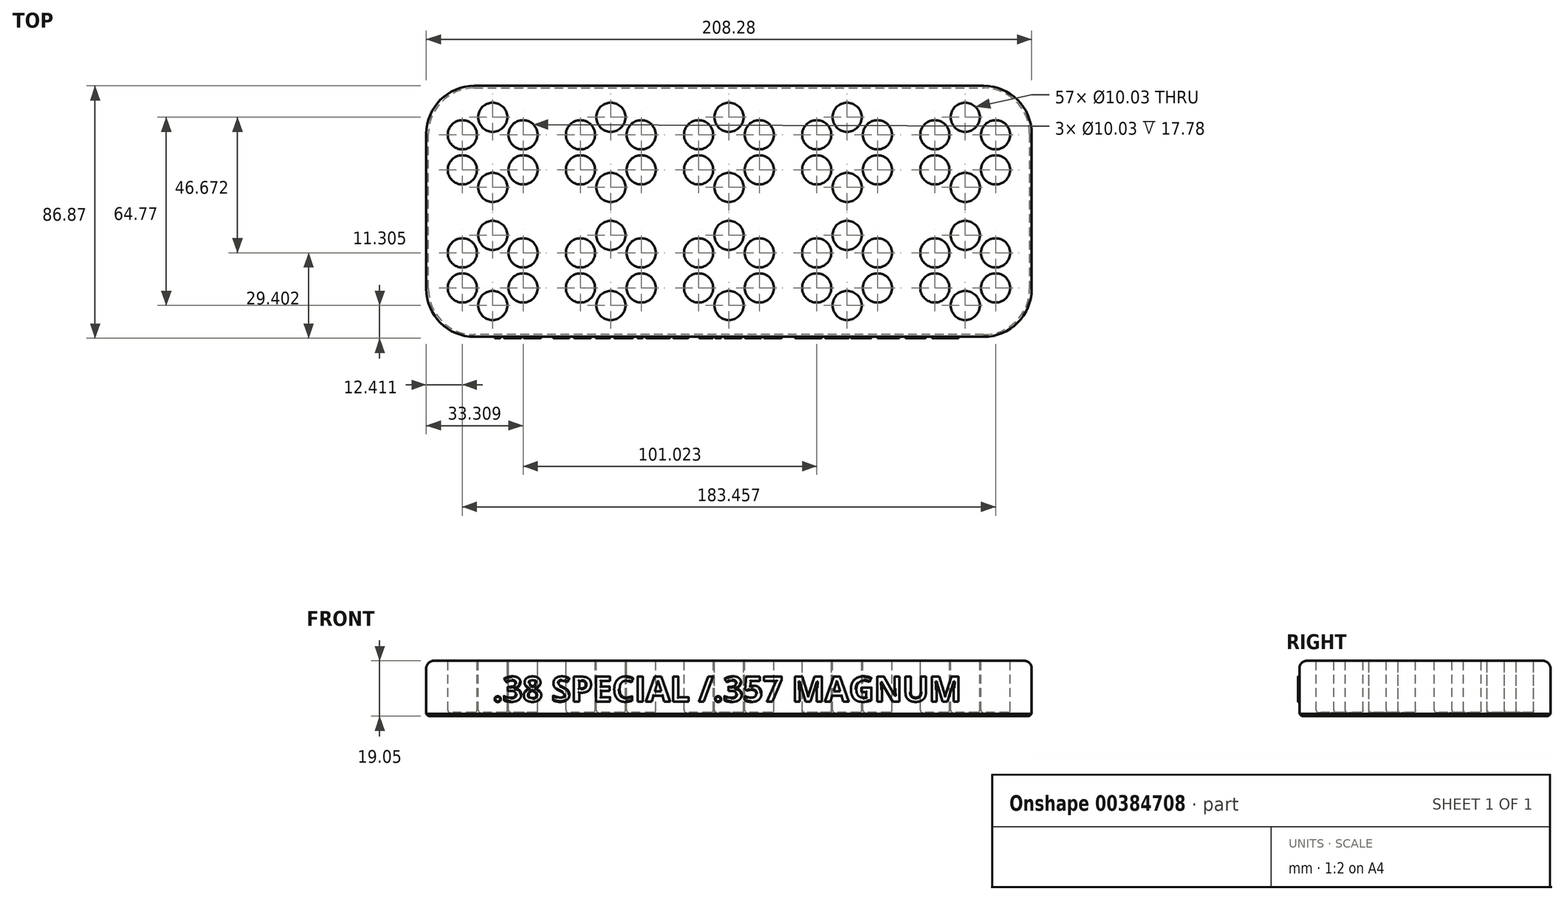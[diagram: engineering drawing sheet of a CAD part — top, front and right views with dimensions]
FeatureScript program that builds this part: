
annotation { "Feature Type Name" : "Feature", "Feature Type Description" : "" }
export const myFeature = defineFeature(function(context is Context, id is Id, definition is map)
    precondition{}
    {
        {
            var Q0;
            Q0=qCreatedBy(makeId("Top.planeOp"),FACE);
            var sketch = newSketch(context, id + "F0", { "sketchPlane" : qUnion([Q0])});
            skLineSegment(sketch, "E0.bottom", {"start": v(-106.68, 50.8) * mm, "end": v(101.6, 50.8) * mm});
            skLineSegment(sketch, "E0.top", {"start": v(-106.68, -35.56) * mm, "end": v(101.6, -35.56) * mm});
            skLineSegment(sketch, "E0.left", {"start": v(-106.68, 50.8) * mm, "end": v(-106.68, -35.56) * mm});
            skLineSegment(sketch, "E0.right", {"start": v(101.6, 50.8) * mm, "end": v(101.6, -35.56) * mm});
            skSolve(sketch);
        }
        {
            var Q0;
            Q0=qSketchRegion(id+"F0",true);
            extrude(context, id + "F1", {"entities" : qUnion([Q0]), "depth" : 19.05 * mm});
        }
        {
            var Q0;
            Q0=makeQuery(id+"F1.opExtrude","CAP_FACE",FACE,{"disambiguationData":[OSD([sQuery(id+"F0.wireOp",EDGE,"E0.bottom"),sQuery(id+"F0.wireOp",EDGE,"E0.top"),sQuery(id+"F0.wireOp",EDGE,"E0.left"),sQuery(id+"F0.wireOp",EDGE,"E0.right")])],"isStart":false});
            var sketch = newSketch(context, id + "F2", { "sketchPlane" : qUnion([Q0])});
            skCircle(sketch, "E1", {"center": v(-83.82, 27.94) * mm, "radius": 18.41 * mm});
            skCircle(sketch, "E2", {"center": v(-83.82, -12.7) * mm, "radius": 18.41 * mm});
            skCircle(sketch, "E3.1.0.0", {"center": v(-43.18, -12.7) * mm, "radius": 18.41 * mm});
            skCircle(sketch, "E3.1.0.1", {"center": v(-43.18, 27.94) * mm, "radius": 18.41 * mm});
            skCircle(sketch, "E3.2.0.0", {"center": v(-2.54, -12.7) * mm, "radius": 18.41 * mm});
            skCircle(sketch, "E3.2.0.1", {"center": v(-2.54, 27.94) * mm, "radius": 18.41 * mm});
            skCircle(sketch, "E3.3.0.0", {"center": v(38.1, -12.7) * mm, "radius": 18.41 * mm});
            skCircle(sketch, "E3.3.0.1", {"center": v(38.1, 27.94) * mm, "radius": 18.41 * mm});
            skCircle(sketch, "E3.4.0.0", {"center": v(78.74, -12.7) * mm, "radius": 18.41 * mm});
            skCircle(sketch, "E3.4.0.1", {"center": v(78.74, 27.94) * mm, "radius": 18.41 * mm});
            skLineSegment(sketch, "E3.direction1", {"start": v(-83.82, -12.7) * mm, "end": v(-43.18, -12.7) * mm, "construction": true});
            skSolve(sketch);
        }
        {
            var Q0;
            Q0=makeQuery(id+"F2.imprint","IMPRINT",FACE,{"disambiguationData":[TD([[makeQuery(id+"F2.imprint","IMPRINT",EDGE,{"derivedFrom":sQuery(id+"F2.wireOp",EDGE,"E1")}),-1.0]])]});
            var sketch = newSketch(context, id + "F3", { "sketchPlane" : qUnion([Q0])});
            skCircle(sketch, "E4", {"center": v(-83.82, 40) * mm, "radius": 5.02 * mm});
            skCircle(sketch, "E5.1.0", {"center": v(-94.27, 33.97) * mm, "radius": 5.02 * mm});
            skCircle(sketch, "E5.2.0", {"center": v(-94.27, 21.9) * mm, "radius": 5.02 * mm});
            skCircle(sketch, "E5.3.0", {"center": v(-83.82, 15.87) * mm, "radius": 5.02 * mm});
            skCircle(sketch, "E5.4.0", {"center": v(-73.37, 21.9) * mm, "radius": 5.02 * mm});
            skPoint(sketch, "E5.center", {"position": v(-83.82, 27.94) * mm});
            skCircle(sketch, "E6.1.5.0", {"center": v(-73.37, 33.97) * mm, "radius": 5.02 * mm});
            skCircle(sketch, "E7.0.1.0", {"center": v(-83.82, -0.64) * mm, "radius": 5.02 * mm});
            skCircle(sketch, "E7.0.1.1", {"center": v(-83.82, -24.77) * mm, "radius": 5.02 * mm});
            skCircle(sketch, "E7.0.1.2", {"center": v(-94.27, -6.67) * mm, "radius": 5.02 * mm});
            skCircle(sketch, "E7.0.1.3", {"center": v(-73.37, -18.73) * mm, "radius": 5.02 * mm});
            skPoint(sketch, "E7.0.1.4", {"position": v(-83.82, -12.7) * mm});
            skCircle(sketch, "E7.0.1.5", {"center": v(-94.27, -18.73) * mm, "radius": 5.02 * mm});
            skCircle(sketch, "E7.0.1.6", {"center": v(-73.37, -6.67) * mm, "radius": 5.02 * mm});
            skCircle(sketch, "E7.1.0.0", {"center": v(-43.18, 40) * mm, "radius": 5.02 * mm});
            skCircle(sketch, "E7.1.0.1", {"center": v(-43.18, 15.87) * mm, "radius": 5.02 * mm});
            skCircle(sketch, "E7.1.0.2", {"center": v(-53.63, 33.97) * mm, "radius": 5.02 * mm});
            skCircle(sketch, "E7.1.0.3", {"center": v(-32.73, 21.9) * mm, "radius": 5.02 * mm});
            skPoint(sketch, "E7.1.0.4", {"position": v(-43.18, 27.94) * mm});
            skCircle(sketch, "E7.1.0.5", {"center": v(-53.63, 21.9) * mm, "radius": 5.02 * mm});
            skCircle(sketch, "E7.1.0.6", {"center": v(-32.73, 33.97) * mm, "radius": 5.02 * mm});
            skCircle(sketch, "E7.1.1.0", {"center": v(-43.18, -0.64) * mm, "radius": 5.02 * mm});
            skCircle(sketch, "E7.1.1.1", {"center": v(-43.18, -24.77) * mm, "radius": 5.02 * mm});
            skCircle(sketch, "E7.1.1.2", {"center": v(-53.63, -6.67) * mm, "radius": 5.02 * mm});
            skCircle(sketch, "E7.1.1.3", {"center": v(-32.73, -18.73) * mm, "radius": 5.02 * mm});
            skPoint(sketch, "E7.1.1.4", {"position": v(-43.18, -12.7) * mm});
            skCircle(sketch, "E7.1.1.5", {"center": v(-53.63, -18.73) * mm, "radius": 5.02 * mm});
            skCircle(sketch, "E7.1.1.6", {"center": v(-32.73, -6.67) * mm, "radius": 5.02 * mm});
            skCircle(sketch, "E7.2.0.0", {"center": v(-2.54, 40) * mm, "radius": 5.02 * mm});
            skCircle(sketch, "E7.2.0.1", {"center": v(-2.54, 15.87) * mm, "radius": 5.02 * mm});
            skCircle(sketch, "E7.2.0.2", {"center": v(-12.99, 33.97) * mm, "radius": 5.02 * mm});
            skCircle(sketch, "E7.2.0.3", {"center": v(7.9, 21.9) * mm, "radius": 5.02 * mm});
            skPoint(sketch, "E7.2.0.4", {"position": v(-2.54, 27.94) * mm});
            skCircle(sketch, "E7.2.0.5", {"center": v(-12.99, 21.9) * mm, "radius": 5.02 * mm});
            skCircle(sketch, "E7.2.0.6", {"center": v(7.9, 33.97) * mm, "radius": 5.02 * mm});
            skCircle(sketch, "E7.2.1.0", {"center": v(-2.54, -0.64) * mm, "radius": 5.02 * mm});
            skCircle(sketch, "E7.2.1.1", {"center": v(-2.54, -24.77) * mm, "radius": 5.02 * mm});
            skCircle(sketch, "E7.2.1.2", {"center": v(-12.99, -6.67) * mm, "radius": 5.02 * mm});
            skCircle(sketch, "E7.2.1.3", {"center": v(7.9, -18.73) * mm, "radius": 5.02 * mm});
            skPoint(sketch, "E7.2.1.4", {"position": v(-2.54, -12.7) * mm});
            skCircle(sketch, "E7.2.1.5", {"center": v(-12.99, -18.73) * mm, "radius": 5.02 * mm});
            skCircle(sketch, "E7.2.1.6", {"center": v(7.9, -6.67) * mm, "radius": 5.02 * mm});
            skCircle(sketch, "E7.3.0.0", {"center": v(38.1, 40) * mm, "radius": 5.02 * mm});
            skCircle(sketch, "E7.3.0.1", {"center": v(38.1, 15.87) * mm, "radius": 5.02 * mm});
            skCircle(sketch, "E7.3.0.2", {"center": v(27.65, 33.97) * mm, "radius": 5.02 * mm});
            skCircle(sketch, "E7.3.0.3", {"center": v(48.55, 21.9) * mm, "radius": 5.02 * mm});
            skPoint(sketch, "E7.3.0.4", {"position": v(38.1, 27.94) * mm});
            skCircle(sketch, "E7.3.0.5", {"center": v(27.65, 21.9) * mm, "radius": 5.02 * mm});
            skCircle(sketch, "E7.3.0.6", {"center": v(48.55, 33.97) * mm, "radius": 5.02 * mm});
            skCircle(sketch, "E7.3.1.0", {"center": v(38.1, -0.64) * mm, "radius": 5.02 * mm});
            skCircle(sketch, "E7.3.1.1", {"center": v(38.1, -24.77) * mm, "radius": 5.02 * mm});
            skCircle(sketch, "E7.3.1.2", {"center": v(27.65, -6.67) * mm, "radius": 5.02 * mm});
            skCircle(sketch, "E7.3.1.3", {"center": v(48.55, -18.73) * mm, "radius": 5.02 * mm});
            skPoint(sketch, "E7.3.1.4", {"position": v(38.1, -12.7) * mm});
            skCircle(sketch, "E7.3.1.5", {"center": v(27.65, -18.73) * mm, "radius": 5.02 * mm});
            skCircle(sketch, "E7.3.1.6", {"center": v(48.55, -6.67) * mm, "radius": 5.02 * mm});
            skCircle(sketch, "E7.4.0.0", {"center": v(78.74, 40) * mm, "radius": 5.02 * mm});
            skCircle(sketch, "E7.4.0.1", {"center": v(78.74, 15.87) * mm, "radius": 5.02 * mm});
            skCircle(sketch, "E7.4.0.2", {"center": v(68.3, 33.97) * mm, "radius": 5.02 * mm});
            skCircle(sketch, "E7.4.0.3", {"center": v(89.19, 21.9) * mm, "radius": 5.02 * mm});
            skPoint(sketch, "E7.4.0.4", {"position": v(78.74, 27.94) * mm});
            skCircle(sketch, "E7.4.0.5", {"center": v(68.3, 21.9) * mm, "radius": 5.02 * mm});
            skCircle(sketch, "E7.4.0.6", {"center": v(89.19, 33.97) * mm, "radius": 5.02 * mm});
            skCircle(sketch, "E7.4.1.0", {"center": v(78.74, -0.64) * mm, "radius": 5.02 * mm});
            skCircle(sketch, "E7.4.1.1", {"center": v(78.74, -24.77) * mm, "radius": 5.02 * mm});
            skCircle(sketch, "E7.4.1.2", {"center": v(68.3, -6.67) * mm, "radius": 5.02 * mm});
            skCircle(sketch, "E7.4.1.3", {"center": v(89.19, -18.73) * mm, "radius": 5.02 * mm});
            skPoint(sketch, "E7.4.1.4", {"position": v(78.74, -12.7) * mm});
            skCircle(sketch, "E7.4.1.5", {"center": v(68.3, -18.73) * mm, "radius": 5.02 * mm});
            skCircle(sketch, "E7.4.1.6", {"center": v(89.19, -6.67) * mm, "radius": 5.02 * mm});
            skLineSegment(sketch, "E7.direction1", {"start": v(-94.27, 21.9) * mm, "end": v(-53.63, 21.9) * mm, "construction": true});
            skLineSegment(sketch, "E7.direction2", {"start": v(-94.27, 21.9) * mm, "end": v(-94.27, -18.73) * mm, "construction": true});
            skSolve(sketch);
        }
        {
            var Q0;
            Q0=qSketchRegion(id+"F3",true);
            extrude(context, id + "F4", {"entities" : qUnion([Q0]), "operationType" : NewBodyOperationType.REMOVE, "oppositeDirection" : true, "depth" : 17.78 * mm});
        }
        {
            var Q0;
            Q0=makeQuery(id+"F1.opExtrude","SWEPT_EDGE",EDGE,{"disambiguationData":[OSD([sQuery(id+"F0.wireOp",EDGE,"E0.top"),sQuery(id+"F0.wireOp",EDGE,"E0.left")])]});
            var Q1;
            Q1=makeQuery(id+"F1.opExtrude","SWEPT_EDGE",EDGE,{"disambiguationData":[OSD([sQuery(id+"F0.wireOp",EDGE,"E0.bottom"),sQuery(id+"F0.wireOp",EDGE,"E0.left")])]});
            var Q2;
            Q2=makeQuery(id+"F1.opExtrude","SWEPT_EDGE",EDGE,{"disambiguationData":[OSD([sQuery(id+"F0.wireOp",EDGE,"E0.bottom"),sQuery(id+"F0.wireOp",EDGE,"E0.right")])]});
            var Q3;
            Q3=makeQuery(id+"F1.opExtrude","SWEPT_EDGE",EDGE,{"disambiguationData":[OSD([sQuery(id+"F0.wireOp",EDGE,"E0.top"),sQuery(id+"F0.wireOp",EDGE,"E0.right")])]});
            fillet(context, id + "F5", {"entities" : qUnion([Q0, Q1, Q2, Q3]), "radius" : 16.5 * mm, "tangentPropagation" : true, "allowEdgeOverflow" : false});
        }
        {
            var Q0;
            Q0=makeQuery(id+"F1.opExtrude","CAP_EDGE",EDGE,{"disambiguationData":[OSD([sQuery(id+"F0.wireOp",EDGE,"E0.bottom")])],"isStart":false});
            fillet(context, id + "F6", {"entities" : qUnion([Q0]), "radius" : 2.54 * mm, "tangentPropagation" : true, "allowEdgeOverflow" : false});
        }
        {
            var Q0;
            Q0=makeQuery(id+"F4.boolean.opBoolean","COPY",EDGE,{"derivedFrom":makeQuery(id+"F4.opExtrude","CAP_EDGE",EDGE,{"disambiguationData":[OSD([sQuery(id+"F3.wireOp",EDGE,"d77acf85-acbb-40a3-aece-45e6eb51fefa.2.0.3")])],"isStart":true})});
            var Q1;
            Q1=makeQuery(id+"F4.boolean.opBoolean","COPY",EDGE,{"derivedFrom":makeQuery(id+"F4.opExtrude","CAP_EDGE",EDGE,{"disambiguationData":[OSD([sQuery(id+"F3.wireOp",EDGE,"d77acf85-acbb-40a3-aece-45e6eb51fefa.1.0.3")])],"isStart":true})});
            var Q2;
            Q2=makeQuery(id+"F4.boolean.opBoolean","COPY",EDGE,{"derivedFrom":makeQuery(id+"F4.opExtrude","CAP_EDGE",EDGE,{"disambiguationData":[OSD([sQuery(id+"F3.wireOp",EDGE,"d77acf85-acbb-40a3-aece-45e6eb51fefa.4.0.3")])],"isStart":true})});
            var Q3;
            Q3=makeQuery(id+"F4.boolean.opBoolean","COPY",EDGE,{"derivedFrom":makeQuery(id+"F4.opExtrude","CAP_EDGE",EDGE,{"disambiguationData":[OSD([sQuery(id+"F3.wireOp",EDGE,"d77acf85-acbb-40a3-aece-45e6eb51fefa.4.1.0")])],"isStart":true})});
            var Q4;
            Q4=makeQuery(id+"F4.boolean.opBoolean","COPY",EDGE,{"derivedFrom":makeQuery(id+"F4.opExtrude","CAP_EDGE",EDGE,{"disambiguationData":[OSD([sQuery(id+"F3.wireOp",EDGE,"d77acf85-acbb-40a3-aece-45e6eb51fefa.4.0.2")])],"isStart":true})});
            var Q5;
            Q5=makeQuery(id+"F4.boolean.opBoolean","COPY",EDGE,{"derivedFrom":makeQuery(id+"F4.opExtrude","CAP_EDGE",EDGE,{"disambiguationData":[OSD([sQuery(id+"F3.wireOp",EDGE,"d77acf85-acbb-40a3-aece-45e6eb51fefa.4.0.0")])],"isStart":true})});
            var Q6;
            Q6=makeQuery(id+"F4.boolean.opBoolean","COPY",EDGE,{"derivedFrom":makeQuery(id+"F4.opExtrude","CAP_EDGE",EDGE,{"disambiguationData":[OSD([sQuery(id+"F3.wireOp",EDGE,"d77acf85-acbb-40a3-aece-45e6eb51fefa.0.1.5")])],"isStart":true})});
            var Q7;
            Q7=makeQuery(id+"F4.boolean.opBoolean","COPY",EDGE,{"derivedFrom":makeQuery(id+"F4.opExtrude","CAP_EDGE",EDGE,{"disambiguationData":[OSD([sQuery(id+"F3.wireOp",EDGE,"d77acf85-acbb-40a3-aece-45e6eb51fefa.2.0.0")])],"isStart":true})});
            var Q8;
            Q8=makeQuery(id+"F4.boolean.opBoolean","COPY",EDGE,{"derivedFrom":makeQuery(id+"F4.opExtrude","CAP_EDGE",EDGE,{"disambiguationData":[OSD([sQuery(id+"F3.wireOp",EDGE,"E4")])],"isStart":true})});
            var Q9;
            Q9=makeQuery(id+"F4.boolean.opBoolean","COPY",EDGE,{"derivedFrom":makeQuery(id+"F4.opExtrude","CAP_EDGE",EDGE,{"disambiguationData":[OSD([sQuery(id+"F3.wireOp",EDGE,"d77acf85-acbb-40a3-aece-45e6eb51fefa.2.1.0")])],"isStart":true})});
            var Q10;
            Q10=makeQuery(id+"F4.boolean.opBoolean","COPY",EDGE,{"derivedFrom":makeQuery(id+"F4.opExtrude","CAP_EDGE",EDGE,{"disambiguationData":[OSD([sQuery(id+"F3.wireOp",EDGE,"d77acf85-acbb-40a3-aece-45e6eb51fefa.1.1.3")])],"isStart":true})});
            var Q11;
            Q11=makeQuery(id+"F4.boolean.opBoolean","COPY",EDGE,{"derivedFrom":makeQuery(id+"F4.opExtrude","CAP_EDGE",EDGE,{"disambiguationData":[OSD([sQuery(id+"F3.wireOp",EDGE,"d77acf85-acbb-40a3-aece-45e6eb51fefa.2.1.2")])],"isStart":true})});
            var Q12;
            Q12=makeQuery(id+"F4.boolean.opBoolean","COPY",EDGE,{"derivedFrom":makeQuery(id+"F4.opExtrude","CAP_EDGE",EDGE,{"disambiguationData":[OSD([sQuery(id+"F3.wireOp",EDGE,"E5.4.0")])],"isStart":true})});
            var Q13;
            Q13=makeQuery(id+"F4.boolean.opBoolean","COPY",EDGE,{"derivedFrom":makeQuery(id+"F4.opExtrude","CAP_EDGE",EDGE,{"disambiguationData":[OSD([sQuery(id+"F3.wireOp",EDGE,"E5.3.0")])],"isStart":true})});
            var Q14;
            Q14=makeQuery(id+"F4.boolean.opBoolean","COPY",EDGE,{"derivedFrom":makeQuery(id+"F4.opExtrude","CAP_EDGE",EDGE,{"disambiguationData":[OSD([sQuery(id+"F3.wireOp",EDGE,"d77acf85-acbb-40a3-aece-45e6eb51fefa.3.1.4")])],"isStart":true})});
            var Q15;
            Q15=makeQuery(id+"F4.boolean.opBoolean","COPY",EDGE,{"derivedFrom":makeQuery(id+"F4.opExtrude","CAP_EDGE",EDGE,{"disambiguationData":[OSD([sQuery(id+"F3.wireOp",EDGE,"d77acf85-acbb-40a3-aece-45e6eb51fefa.1.0.5")])],"isStart":true})});
            var Q16;
            Q16=makeQuery(id+"F4.boolean.opBoolean","COPY",EDGE,{"derivedFrom":makeQuery(id+"F4.opExtrude","CAP_EDGE",EDGE,{"disambiguationData":[OSD([sQuery(id+"F3.wireOp",EDGE,"d77acf85-acbb-40a3-aece-45e6eb51fefa.1.0.4")])],"isStart":true})});
            var Q17;
            Q17=makeQuery(id+"F4.boolean.opBoolean","COPY",EDGE,{"derivedFrom":makeQuery(id+"F4.opExtrude","CAP_EDGE",EDGE,{"disambiguationData":[OSD([sQuery(id+"F3.wireOp",EDGE,"d77acf85-acbb-40a3-aece-45e6eb51fefa.2.1.3")])],"isStart":true})});
            var Q18;
            Q18=makeQuery(id+"F4.boolean.opBoolean","COPY",EDGE,{"derivedFrom":makeQuery(id+"F4.opExtrude","CAP_EDGE",EDGE,{"disambiguationData":[OSD([sQuery(id+"F3.wireOp",EDGE,"d77acf85-acbb-40a3-aece-45e6eb51fefa.1.1.4")])],"isStart":true})});
            var Q19;
            Q19=makeQuery(id+"F4.boolean.opBoolean","COPY",EDGE,{"derivedFrom":makeQuery(id+"F4.opExtrude","CAP_EDGE",EDGE,{"disambiguationData":[OSD([sQuery(id+"F3.wireOp",EDGE,"d77acf85-acbb-40a3-aece-45e6eb51fefa.3.0.2")])],"isStart":true})});
            var Q20;
            Q20=makeQuery(id+"F4.boolean.opBoolean","COPY",EDGE,{"derivedFrom":makeQuery(id+"F4.opExtrude","CAP_EDGE",EDGE,{"disambiguationData":[OSD([sQuery(id+"F3.wireOp",EDGE,"d77acf85-acbb-40a3-aece-45e6eb51fefa.3.1.5")])],"isStart":true})});
            var Q21;
            Q21=makeQuery(id+"F4.boolean.opBoolean","COPY",EDGE,{"derivedFrom":makeQuery(id+"F4.opExtrude","CAP_EDGE",EDGE,{"disambiguationData":[OSD([sQuery(id+"F3.wireOp",EDGE,"d77acf85-acbb-40a3-aece-45e6eb51fefa.4.1.3")])],"isStart":true})});
            var Q22;
            Q22=makeQuery(id+"F4.boolean.opBoolean","COPY",EDGE,{"derivedFrom":makeQuery(id+"F4.opExtrude","CAP_EDGE",EDGE,{"disambiguationData":[OSD([sQuery(id+"F3.wireOp",EDGE,"d77acf85-acbb-40a3-aece-45e6eb51fefa.2.1.5")])],"isStart":true})});
            var Q23;
            Q23=makeQuery(id+"F4.boolean.opBoolean","COPY",EDGE,{"derivedFrom":makeQuery(id+"F4.opExtrude","CAP_EDGE",EDGE,{"disambiguationData":[OSD([sQuery(id+"F3.wireOp",EDGE,"d77acf85-acbb-40a3-aece-45e6eb51fefa.4.1.2")])],"isStart":true})});
            var Q24;
            Q24=makeQuery(id+"F4.boolean.opBoolean","COPY",EDGE,{"derivedFrom":makeQuery(id+"F4.opExtrude","CAP_EDGE",EDGE,{"disambiguationData":[OSD([sQuery(id+"F3.wireOp",EDGE,"d77acf85-acbb-40a3-aece-45e6eb51fefa.2.0.2")])],"isStart":true})});
            var Q25;
            Q25=makeQuery(id+"F4.boolean.opBoolean","COPY",EDGE,{"derivedFrom":makeQuery(id+"F4.opExtrude","CAP_EDGE",EDGE,{"disambiguationData":[OSD([sQuery(id+"F3.wireOp",EDGE,"d77acf85-acbb-40a3-aece-45e6eb51fefa.1.1.5")])],"isStart":true})});
            var Q26;
            Q26=makeQuery(id+"F4.boolean.opBoolean","COPY",EDGE,{"derivedFrom":makeQuery(id+"F4.opExtrude","CAP_EDGE",EDGE,{"disambiguationData":[OSD([sQuery(id+"F3.wireOp",EDGE,"d77acf85-acbb-40a3-aece-45e6eb51fefa.3.0.0")])],"isStart":true})});
            var Q27;
            Q27=makeQuery(id+"F4.boolean.opBoolean","COPY",EDGE,{"derivedFrom":makeQuery(id+"F4.opExtrude","CAP_EDGE",EDGE,{"disambiguationData":[OSD([sQuery(id+"F3.wireOp",EDGE,"d77acf85-acbb-40a3-aece-45e6eb51fefa.2.0.5")])],"isStart":true})});
            var Q28;
            Q28=makeQuery(id+"F4.boolean.opBoolean","COPY",EDGE,{"derivedFrom":makeQuery(id+"F4.opExtrude","CAP_EDGE",EDGE,{"disambiguationData":[OSD([sQuery(id+"F3.wireOp",EDGE,"d77acf85-acbb-40a3-aece-45e6eb51fefa.0.1.0")])],"isStart":true})});
            var Q29;
            Q29=makeQuery(id+"F4.boolean.opBoolean","COPY",EDGE,{"derivedFrom":makeQuery(id+"F4.opExtrude","CAP_EDGE",EDGE,{"disambiguationData":[OSD([sQuery(id+"F3.wireOp",EDGE,"d77acf85-acbb-40a3-aece-45e6eb51fefa.4.0.4")])],"isStart":true})});
            var Q30;
            Q30=makeQuery(id+"F4.boolean.opBoolean","COPY",EDGE,{"derivedFrom":makeQuery(id+"F4.opExtrude","CAP_EDGE",EDGE,{"disambiguationData":[OSD([sQuery(id+"F3.wireOp",EDGE,"d77acf85-acbb-40a3-aece-45e6eb51fefa.4.0.5")])],"isStart":true})});
            var Q31;
            Q31=makeQuery(id+"F4.boolean.opBoolean","COPY",EDGE,{"derivedFrom":makeQuery(id+"F4.opExtrude","CAP_EDGE",EDGE,{"disambiguationData":[OSD([sQuery(id+"F3.wireOp",EDGE,"d77acf85-acbb-40a3-aece-45e6eb51fefa.3.0.3")])],"isStart":true})});
            var Q32;
            Q32=makeQuery(id+"F4.boolean.opBoolean","COPY",EDGE,{"derivedFrom":makeQuery(id+"F4.opExtrude","CAP_EDGE",EDGE,{"disambiguationData":[OSD([sQuery(id+"F3.wireOp",EDGE,"d77acf85-acbb-40a3-aece-45e6eb51fefa.4.1.4")])],"isStart":true})});
            var Q33;
            Q33=makeQuery(id+"F4.boolean.opBoolean","COPY",EDGE,{"derivedFrom":makeQuery(id+"F4.opExtrude","CAP_EDGE",EDGE,{"disambiguationData":[OSD([sQuery(id+"F3.wireOp",EDGE,"d77acf85-acbb-40a3-aece-45e6eb51fefa.3.1.2")])],"isStart":true})});
            var Q34;
            Q34=makeQuery(id+"F4.boolean.opBoolean","COPY",EDGE,{"derivedFrom":makeQuery(id+"F4.opExtrude","CAP_EDGE",EDGE,{"disambiguationData":[OSD([sQuery(id+"F3.wireOp",EDGE,"E5.2.0")])],"isStart":true})});
            var Q35;
            Q35=makeQuery(id+"F4.boolean.opBoolean","COPY",EDGE,{"derivedFrom":makeQuery(id+"F4.opExtrude","CAP_EDGE",EDGE,{"disambiguationData":[OSD([sQuery(id+"F3.wireOp",EDGE,"d77acf85-acbb-40a3-aece-45e6eb51fefa.0.1.2")])],"isStart":true})});
            var Q36;
            Q36=makeQuery(id+"F4.boolean.opBoolean","COPY",EDGE,{"derivedFrom":makeQuery(id+"F4.opExtrude","CAP_EDGE",EDGE,{"disambiguationData":[OSD([sQuery(id+"F3.wireOp",EDGE,"d77acf85-acbb-40a3-aece-45e6eb51fefa.1.0.2")])],"isStart":true})});
            var Q37;
            Q37=makeQuery(id+"F4.boolean.opBoolean","COPY",EDGE,{"derivedFrom":makeQuery(id+"F4.opExtrude","CAP_EDGE",EDGE,{"disambiguationData":[OSD([sQuery(id+"F3.wireOp",EDGE,"d77acf85-acbb-40a3-aece-45e6eb51fefa.1.1.0")])],"isStart":true})});
            var Q38;
            Q38=makeQuery(id+"F4.boolean.opBoolean","COPY",EDGE,{"derivedFrom":makeQuery(id+"F4.opExtrude","CAP_EDGE",EDGE,{"disambiguationData":[OSD([sQuery(id+"F3.wireOp",EDGE,"d77acf85-acbb-40a3-aece-45e6eb51fefa.2.0.4")])],"isStart":true})});
            var Q39;
            Q39=makeQuery(id+"F4.boolean.opBoolean","COPY",EDGE,{"derivedFrom":makeQuery(id+"F4.opExtrude","CAP_EDGE",EDGE,{"disambiguationData":[OSD([sQuery(id+"F3.wireOp",EDGE,"d77acf85-acbb-40a3-aece-45e6eb51fefa.2.1.4")])],"isStart":true})});
            var Q40;
            Q40=makeQuery(id+"F4.boolean.opBoolean","COPY",EDGE,{"derivedFrom":makeQuery(id+"F4.opExtrude","CAP_EDGE",EDGE,{"disambiguationData":[OSD([sQuery(id+"F3.wireOp",EDGE,"d77acf85-acbb-40a3-aece-45e6eb51fefa.1.0.0")])],"isStart":true})});
            var Q41;
            Q41=makeQuery(id+"F4.boolean.opBoolean","COPY",EDGE,{"derivedFrom":makeQuery(id+"F4.opExtrude","CAP_EDGE",EDGE,{"disambiguationData":[OSD([sQuery(id+"F3.wireOp",EDGE,"d77acf85-acbb-40a3-aece-45e6eb51fefa.1.1.2")])],"isStart":true})});
            var Q42;
            Q42=makeQuery(id+"F4.boolean.opBoolean","COPY",EDGE,{"derivedFrom":makeQuery(id+"F4.opExtrude","CAP_EDGE",EDGE,{"disambiguationData":[OSD([sQuery(id+"F3.wireOp",EDGE,"d77acf85-acbb-40a3-aece-45e6eb51fefa.0.1.3")])],"isStart":true})});
            var Q43;
            Q43=makeQuery(id+"F4.boolean.opBoolean","COPY",EDGE,{"derivedFrom":makeQuery(id+"F4.opExtrude","CAP_EDGE",EDGE,{"disambiguationData":[OSD([sQuery(id+"F3.wireOp",EDGE,"d77acf85-acbb-40a3-aece-45e6eb51fefa.4.1.5")])],"isStart":true})});
            var Q44;
            Q44=makeQuery(id+"F4.boolean.opBoolean","COPY",EDGE,{"derivedFrom":makeQuery(id+"F4.opExtrude","CAP_EDGE",EDGE,{"disambiguationData":[OSD([sQuery(id+"F3.wireOp",EDGE,"d77acf85-acbb-40a3-aece-45e6eb51fefa.3.0.4")])],"isStart":true})});
            var Q45;
            Q45=makeQuery(id+"F4.boolean.opBoolean","COPY",EDGE,{"derivedFrom":makeQuery(id+"F4.opExtrude","CAP_EDGE",EDGE,{"disambiguationData":[OSD([sQuery(id+"F3.wireOp",EDGE,"d77acf85-acbb-40a3-aece-45e6eb51fefa.3.0.5")])],"isStart":true})});
            var Q46;
            Q46=makeQuery(id+"F4.boolean.opBoolean","COPY",EDGE,{"derivedFrom":makeQuery(id+"F4.opExtrude","CAP_EDGE",EDGE,{"disambiguationData":[OSD([sQuery(id+"F3.wireOp",EDGE,"d77acf85-acbb-40a3-aece-45e6eb51fefa.3.1.0")])],"isStart":true})});
            var Q47;
            Q47=makeQuery(id+"F4.boolean.opBoolean","COPY",EDGE,{"derivedFrom":makeQuery(id+"F4.opExtrude","CAP_EDGE",EDGE,{"disambiguationData":[OSD([sQuery(id+"F3.wireOp",EDGE,"d77acf85-acbb-40a3-aece-45e6eb51fefa.3.1.3")])],"isStart":true})});
            var Q48;
            Q48=makeQuery(id+"F4.boolean.opBoolean","COPY",EDGE,{"derivedFrom":makeQuery(id+"F4.opExtrude","CAP_EDGE",EDGE,{"disambiguationData":[OSD([sQuery(id+"F3.wireOp",EDGE,"d77acf85-acbb-40a3-aece-45e6eb51fefa.0.1.2")])],"isStart":false})});
            var Q49;
            Q49=makeQuery(id+"F4.boolean.opBoolean","COPY",EDGE,{"derivedFrom":makeQuery(id+"F4.opExtrude","CAP_EDGE",EDGE,{"disambiguationData":[OSD([sQuery(id+"F3.wireOp",EDGE,"d77acf85-acbb-40a3-aece-45e6eb51fefa.0.1.3")])],"isStart":false})});
            var Q50;
            Q50=makeQuery(id+"F4.boolean.opBoolean","COPY",EDGE,{"derivedFrom":makeQuery(id+"F4.opExtrude","CAP_EDGE",EDGE,{"disambiguationData":[OSD([sQuery(id+"F3.wireOp",EDGE,"E4")])],"isStart":false})});
            var Q51;
            Q51=makeQuery(id+"F4.boolean.opBoolean","COPY",EDGE,{"derivedFrom":makeQuery(id+"F4.opExtrude","CAP_EDGE",EDGE,{"disambiguationData":[OSD([sQuery(id+"F3.wireOp",EDGE,"E5.2.0")])],"isStart":false})});
            var Q52;
            Q52=makeQuery(id+"F4.boolean.opBoolean","COPY",EDGE,{"derivedFrom":makeQuery(id+"F4.opExtrude","CAP_EDGE",EDGE,{"disambiguationData":[OSD([sQuery(id+"F3.wireOp",EDGE,"E5.3.0")])],"isStart":false})});
            var Q53;
            Q53=makeQuery(id+"F4.boolean.opBoolean","COPY",EDGE,{"derivedFrom":makeQuery(id+"F4.opExtrude","CAP_EDGE",EDGE,{"disambiguationData":[OSD([sQuery(id+"F3.wireOp",EDGE,"E5.4.0")])],"isStart":false})});
            var Q54;
            Q54=makeQuery(id+"F4.boolean.opBoolean","COPY",EDGE,{"derivedFrom":makeQuery(id+"F4.opExtrude","CAP_EDGE",EDGE,{"disambiguationData":[OSD([sQuery(id+"F3.wireOp",EDGE,"d77acf85-acbb-40a3-aece-45e6eb51fefa.0.1.0")])],"isStart":false})});
            var Q55;
            Q55=makeQuery(id+"F4.boolean.opBoolean","COPY",EDGE,{"derivedFrom":makeQuery(id+"F4.opExtrude","CAP_EDGE",EDGE,{"disambiguationData":[OSD([sQuery(id+"F3.wireOp",EDGE,"d77acf85-acbb-40a3-aece-45e6eb51fefa.1.0.5")])],"isStart":false})});
            var Q56;
            Q56=makeQuery(id+"F4.boolean.opBoolean","COPY",EDGE,{"derivedFrom":makeQuery(id+"F4.opExtrude","CAP_EDGE",EDGE,{"disambiguationData":[OSD([sQuery(id+"F3.wireOp",EDGE,"d77acf85-acbb-40a3-aece-45e6eb51fefa.2.0.3")])],"isStart":false})});
            var Q57;
            Q57=makeQuery(id+"F4.boolean.opBoolean","COPY",EDGE,{"derivedFrom":makeQuery(id+"F4.opExtrude","CAP_EDGE",EDGE,{"disambiguationData":[OSD([sQuery(id+"F3.wireOp",EDGE,"d77acf85-acbb-40a3-aece-45e6eb51fefa.3.0.0")])],"isStart":false})});
            var Q58;
            Q58=makeQuery(id+"F4.boolean.opBoolean","COPY",EDGE,{"derivedFrom":makeQuery(id+"F4.opExtrude","CAP_EDGE",EDGE,{"disambiguationData":[OSD([sQuery(id+"F3.wireOp",EDGE,"d77acf85-acbb-40a3-aece-45e6eb51fefa.3.1.4")])],"isStart":false})});
            var Q59;
            Q59=makeQuery(id+"F4.boolean.opBoolean","COPY",EDGE,{"derivedFrom":makeQuery(id+"F4.opExtrude","CAP_EDGE",EDGE,{"disambiguationData":[OSD([sQuery(id+"F3.wireOp",EDGE,"d77acf85-acbb-40a3-aece-45e6eb51fefa.4.1.2")])],"isStart":false})});
            var Q60;
            Q60=makeQuery(id+"F4.boolean.opBoolean","COPY",EDGE,{"derivedFrom":makeQuery(id+"F4.opExtrude","CAP_EDGE",EDGE,{"disambiguationData":[OSD([sQuery(id+"F3.wireOp",EDGE,"d77acf85-acbb-40a3-aece-45e6eb51fefa.1.1.0")])],"isStart":false})});
            var Q61;
            Q61=makeQuery(id+"F4.boolean.opBoolean","COPY",EDGE,{"derivedFrom":makeQuery(id+"F4.opExtrude","CAP_EDGE",EDGE,{"disambiguationData":[OSD([sQuery(id+"F3.wireOp",EDGE,"d77acf85-acbb-40a3-aece-45e6eb51fefa.2.0.4")])],"isStart":false})});
            var Q62;
            Q62=makeQuery(id+"F4.boolean.opBoolean","COPY",EDGE,{"derivedFrom":makeQuery(id+"F4.opExtrude","CAP_EDGE",EDGE,{"disambiguationData":[OSD([sQuery(id+"F3.wireOp",EDGE,"d77acf85-acbb-40a3-aece-45e6eb51fefa.3.0.2")])],"isStart":false})});
            var Q63;
            Q63=makeQuery(id+"F4.boolean.opBoolean","COPY",EDGE,{"derivedFrom":makeQuery(id+"F4.opExtrude","CAP_EDGE",EDGE,{"disambiguationData":[OSD([sQuery(id+"F3.wireOp",EDGE,"d77acf85-acbb-40a3-aece-45e6eb51fefa.3.1.5")])],"isStart":false})});
            var Q64;
            Q64=makeQuery(id+"F4.boolean.opBoolean","COPY",EDGE,{"derivedFrom":makeQuery(id+"F4.opExtrude","CAP_EDGE",EDGE,{"disambiguationData":[OSD([sQuery(id+"F3.wireOp",EDGE,"d77acf85-acbb-40a3-aece-45e6eb51fefa.4.1.3")])],"isStart":false})});
            var Q65;
            Q65=makeQuery(id+"F4.boolean.opBoolean","COPY",EDGE,{"derivedFrom":makeQuery(id+"F4.opExtrude","CAP_EDGE",EDGE,{"disambiguationData":[OSD([sQuery(id+"F3.wireOp",EDGE,"d77acf85-acbb-40a3-aece-45e6eb51fefa.1.1.2")])],"isStart":false})});
            var Q66;
            Q66=makeQuery(id+"F4.boolean.opBoolean","COPY",EDGE,{"derivedFrom":makeQuery(id+"F4.opExtrude","CAP_EDGE",EDGE,{"disambiguationData":[OSD([sQuery(id+"F3.wireOp",EDGE,"d77acf85-acbb-40a3-aece-45e6eb51fefa.2.0.5")])],"isStart":false})});
            var Q67;
            Q67=makeQuery(id+"F4.boolean.opBoolean","COPY",EDGE,{"derivedFrom":makeQuery(id+"F4.opExtrude","CAP_EDGE",EDGE,{"disambiguationData":[OSD([sQuery(id+"F3.wireOp",EDGE,"d77acf85-acbb-40a3-aece-45e6eb51fefa.3.0.3")])],"isStart":false})});
            var Q68;
            Q68=makeQuery(id+"F4.boolean.opBoolean","COPY",EDGE,{"derivedFrom":makeQuery(id+"F4.opExtrude","CAP_EDGE",EDGE,{"disambiguationData":[OSD([sQuery(id+"F3.wireOp",EDGE,"d77acf85-acbb-40a3-aece-45e6eb51fefa.4.0.0")])],"isStart":false})});
            var Q69;
            Q69=makeQuery(id+"F4.boolean.opBoolean","COPY",EDGE,{"derivedFrom":makeQuery(id+"F4.opExtrude","CAP_EDGE",EDGE,{"disambiguationData":[OSD([sQuery(id+"F3.wireOp",EDGE,"d77acf85-acbb-40a3-aece-45e6eb51fefa.4.1.4")])],"isStart":false})});
            var Q70;
            Q70=makeQuery(id+"F4.boolean.opBoolean","COPY",EDGE,{"derivedFrom":makeQuery(id+"F4.opExtrude","CAP_EDGE",EDGE,{"disambiguationData":[OSD([sQuery(id+"F3.wireOp",EDGE,"d77acf85-acbb-40a3-aece-45e6eb51fefa.0.1.5")])],"isStart":false})});
            var Q71;
            Q71=makeQuery(id+"F4.boolean.opBoolean","COPY",EDGE,{"derivedFrom":makeQuery(id+"F4.opExtrude","CAP_EDGE",EDGE,{"disambiguationData":[OSD([sQuery(id+"F3.wireOp",EDGE,"d77acf85-acbb-40a3-aece-45e6eb51fefa.1.1.3")])],"isStart":false})});
            var Q72;
            Q72=makeQuery(id+"F4.boolean.opBoolean","COPY",EDGE,{"derivedFrom":makeQuery(id+"F4.opExtrude","CAP_EDGE",EDGE,{"disambiguationData":[OSD([sQuery(id+"F3.wireOp",EDGE,"d77acf85-acbb-40a3-aece-45e6eb51fefa.2.1.0")])],"isStart":false})});
            var Q73;
            Q73=makeQuery(id+"F4.boolean.opBoolean","COPY",EDGE,{"derivedFrom":makeQuery(id+"F4.opExtrude","CAP_EDGE",EDGE,{"disambiguationData":[OSD([sQuery(id+"F3.wireOp",EDGE,"d77acf85-acbb-40a3-aece-45e6eb51fefa.3.0.4")])],"isStart":false})});
            var Q74;
            Q74=makeQuery(id+"F4.boolean.opBoolean","COPY",EDGE,{"derivedFrom":makeQuery(id+"F4.opExtrude","CAP_EDGE",EDGE,{"disambiguationData":[OSD([sQuery(id+"F3.wireOp",EDGE,"d77acf85-acbb-40a3-aece-45e6eb51fefa.4.0.2")])],"isStart":false})});
            var Q75;
            Q75=makeQuery(id+"F4.boolean.opBoolean","COPY",EDGE,{"derivedFrom":makeQuery(id+"F4.opExtrude","CAP_EDGE",EDGE,{"disambiguationData":[OSD([sQuery(id+"F3.wireOp",EDGE,"d77acf85-acbb-40a3-aece-45e6eb51fefa.4.1.5")])],"isStart":false})});
            var Q76;
            Q76=makeQuery(id+"F4.boolean.opBoolean","COPY",EDGE,{"derivedFrom":makeQuery(id+"F4.opExtrude","CAP_EDGE",EDGE,{"disambiguationData":[OSD([sQuery(id+"F3.wireOp",EDGE,"d77acf85-acbb-40a3-aece-45e6eb51fefa.1.0.0")])],"isStart":false})});
            var Q77;
            Q77=makeQuery(id+"F4.boolean.opBoolean","COPY",EDGE,{"derivedFrom":makeQuery(id+"F4.opExtrude","CAP_EDGE",EDGE,{"disambiguationData":[OSD([sQuery(id+"F3.wireOp",EDGE,"d77acf85-acbb-40a3-aece-45e6eb51fefa.1.1.4")])],"isStart":false})});
            var Q78;
            Q78=makeQuery(id+"F4.boolean.opBoolean","COPY",EDGE,{"derivedFrom":makeQuery(id+"F4.opExtrude","CAP_EDGE",EDGE,{"disambiguationData":[OSD([sQuery(id+"F3.wireOp",EDGE,"d77acf85-acbb-40a3-aece-45e6eb51fefa.2.1.2")])],"isStart":false})});
            var Q79;
            Q79=makeQuery(id+"F4.boolean.opBoolean","COPY",EDGE,{"derivedFrom":makeQuery(id+"F4.opExtrude","CAP_EDGE",EDGE,{"disambiguationData":[OSD([sQuery(id+"F3.wireOp",EDGE,"d77acf85-acbb-40a3-aece-45e6eb51fefa.3.0.5")])],"isStart":false})});
            var Q80;
            Q80=makeQuery(id+"F4.boolean.opBoolean","COPY",EDGE,{"derivedFrom":makeQuery(id+"F4.opExtrude","CAP_EDGE",EDGE,{"disambiguationData":[OSD([sQuery(id+"F3.wireOp",EDGE,"d77acf85-acbb-40a3-aece-45e6eb51fefa.4.0.3")])],"isStart":false})});
            var Q81;
            Q81=makeQuery(id+"F4.boolean.opBoolean","COPY",EDGE,{"derivedFrom":makeQuery(id+"F4.opExtrude","CAP_EDGE",EDGE,{"disambiguationData":[OSD([sQuery(id+"F3.wireOp",EDGE,"d77acf85-acbb-40a3-aece-45e6eb51fefa.1.0.2")])],"isStart":false})});
            var Q82;
            Q82=makeQuery(id+"F4.boolean.opBoolean","COPY",EDGE,{"derivedFrom":makeQuery(id+"F4.opExtrude","CAP_EDGE",EDGE,{"disambiguationData":[OSD([sQuery(id+"F3.wireOp",EDGE,"d77acf85-acbb-40a3-aece-45e6eb51fefa.1.1.5")])],"isStart":false})});
            var Q83;
            Q83=makeQuery(id+"F4.boolean.opBoolean","COPY",EDGE,{"derivedFrom":makeQuery(id+"F4.opExtrude","CAP_EDGE",EDGE,{"disambiguationData":[OSD([sQuery(id+"F3.wireOp",EDGE,"d77acf85-acbb-40a3-aece-45e6eb51fefa.2.1.3")])],"isStart":false})});
            var Q84;
            Q84=makeQuery(id+"F4.boolean.opBoolean","COPY",EDGE,{"derivedFrom":makeQuery(id+"F4.opExtrude","CAP_EDGE",EDGE,{"disambiguationData":[OSD([sQuery(id+"F3.wireOp",EDGE,"d77acf85-acbb-40a3-aece-45e6eb51fefa.3.1.0")])],"isStart":false})});
            var Q85;
            Q85=makeQuery(id+"F4.boolean.opBoolean","COPY",EDGE,{"derivedFrom":makeQuery(id+"F4.opExtrude","CAP_EDGE",EDGE,{"disambiguationData":[OSD([sQuery(id+"F3.wireOp",EDGE,"d77acf85-acbb-40a3-aece-45e6eb51fefa.4.0.4")])],"isStart":false})});
            var Q86;
            Q86=makeQuery(id+"F4.boolean.opBoolean","COPY",EDGE,{"derivedFrom":makeQuery(id+"F4.opExtrude","CAP_EDGE",EDGE,{"disambiguationData":[OSD([sQuery(id+"F3.wireOp",EDGE,"d77acf85-acbb-40a3-aece-45e6eb51fefa.1.0.3")])],"isStart":false})});
            var Q87;
            Q87=makeQuery(id+"F4.boolean.opBoolean","COPY",EDGE,{"derivedFrom":makeQuery(id+"F4.opExtrude","CAP_EDGE",EDGE,{"disambiguationData":[OSD([sQuery(id+"F3.wireOp",EDGE,"d77acf85-acbb-40a3-aece-45e6eb51fefa.2.0.0")])],"isStart":false})});
            var Q88;
            Q88=makeQuery(id+"F4.boolean.opBoolean","COPY",EDGE,{"derivedFrom":makeQuery(id+"F4.opExtrude","CAP_EDGE",EDGE,{"disambiguationData":[OSD([sQuery(id+"F3.wireOp",EDGE,"d77acf85-acbb-40a3-aece-45e6eb51fefa.2.1.4")])],"isStart":false})});
            var Q89;
            Q89=makeQuery(id+"F4.boolean.opBoolean","COPY",EDGE,{"derivedFrom":makeQuery(id+"F4.opExtrude","CAP_EDGE",EDGE,{"disambiguationData":[OSD([sQuery(id+"F3.wireOp",EDGE,"d77acf85-acbb-40a3-aece-45e6eb51fefa.3.1.2")])],"isStart":false})});
            var Q90;
            Q90=makeQuery(id+"F4.boolean.opBoolean","COPY",EDGE,{"derivedFrom":makeQuery(id+"F4.opExtrude","CAP_EDGE",EDGE,{"disambiguationData":[OSD([sQuery(id+"F3.wireOp",EDGE,"d77acf85-acbb-40a3-aece-45e6eb51fefa.4.0.5")])],"isStart":false})});
            var Q91;
            Q91=makeQuery(id+"F4.boolean.opBoolean","COPY",EDGE,{"derivedFrom":makeQuery(id+"F4.opExtrude","CAP_EDGE",EDGE,{"disambiguationData":[OSD([sQuery(id+"F3.wireOp",EDGE,"d77acf85-acbb-40a3-aece-45e6eb51fefa.1.0.4")])],"isStart":false})});
            var Q92;
            Q92=makeQuery(id+"F4.boolean.opBoolean","COPY",EDGE,{"derivedFrom":makeQuery(id+"F4.opExtrude","CAP_EDGE",EDGE,{"disambiguationData":[OSD([sQuery(id+"F3.wireOp",EDGE,"d77acf85-acbb-40a3-aece-45e6eb51fefa.2.0.2")])],"isStart":false})});
            var Q93;
            Q93=makeQuery(id+"F4.boolean.opBoolean","COPY",EDGE,{"derivedFrom":makeQuery(id+"F4.opExtrude","CAP_EDGE",EDGE,{"disambiguationData":[OSD([sQuery(id+"F3.wireOp",EDGE,"d77acf85-acbb-40a3-aece-45e6eb51fefa.2.1.5")])],"isStart":false})});
            var Q94;
            Q94=makeQuery(id+"F4.boolean.opBoolean","COPY",EDGE,{"derivedFrom":makeQuery(id+"F4.opExtrude","CAP_EDGE",EDGE,{"disambiguationData":[OSD([sQuery(id+"F3.wireOp",EDGE,"d77acf85-acbb-40a3-aece-45e6eb51fefa.3.1.3")])],"isStart":false})});
            var Q95;
            Q95=makeQuery(id+"F4.boolean.opBoolean","COPY",EDGE,{"derivedFrom":makeQuery(id+"F4.opExtrude","CAP_EDGE",EDGE,{"disambiguationData":[OSD([sQuery(id+"F3.wireOp",EDGE,"d77acf85-acbb-40a3-aece-45e6eb51fefa.4.1.0")])],"isStart":false})});
            var Q96;
            Q96=makeQuery(id+"F4.boolean.opBoolean","COPY",EDGE,{"derivedFrom":makeQuery(id+"F4.opExtrude","CAP_EDGE",EDGE,{"disambiguationData":[OSD([sQuery(id+"F3.wireOp",EDGE,"d77acf85-acbb-40a3-aece-45e6eb51fefa.0.1.4")])],"isStart":true})});
            var Q97;
            Q97=makeQuery(id+"F4.boolean.opBoolean","COPY",EDGE,{"derivedFrom":makeQuery(id+"F4.opExtrude","CAP_EDGE",EDGE,{"disambiguationData":[OSD([sQuery(id+"F3.wireOp",EDGE,"E5.1.0")])],"isStart":true})});
            var Q98;
            Q98=makeQuery(id+"F4.boolean.opBoolean","COPY",EDGE,{"derivedFrom":makeQuery(id+"F4.opExtrude","CAP_EDGE",EDGE,{"disambiguationData":[OSD([sQuery(id+"F3.wireOp",EDGE,"d77acf85-acbb-40a3-aece-45e6eb51fefa.0.1.4")])],"isStart":false})});
            var Q99;
            Q99=makeQuery(id+"F4.boolean.opBoolean","COPY",EDGE,{"derivedFrom":makeQuery(id+"F4.opExtrude","CAP_EDGE",EDGE,{"disambiguationData":[OSD([sQuery(id+"F3.wireOp",EDGE,"E5.1.0")])],"isStart":false})});
            var Q100;
            Q100=makeQuery(id+"F4.boolean.opBoolean","COPY",EDGE,{"derivedFrom":makeQuery(id+"F4.opExtrude","CAP_EDGE",EDGE,{"disambiguationData":[OSD([sQuery(id+"F3.wireOp",EDGE,"E6.1.5.0")])],"isStart":true})});
            var Q101;
            Q101=makeQuery(id+"F4.boolean.opBoolean","COPY",EDGE,{"derivedFrom":makeQuery(id+"F4.opExtrude","CAP_EDGE",EDGE,{"disambiguationData":[OSD([sQuery(id+"F3.wireOp",EDGE,"E7.1.0.2")])],"isStart":true})});
            var Q102;
            Q102=makeQuery(id+"F4.boolean.opBoolean","COPY",EDGE,{"derivedFrom":makeQuery(id+"F4.opExtrude","CAP_EDGE",EDGE,{"disambiguationData":[OSD([sQuery(id+"F3.wireOp",EDGE,"E7.1.0.0")])],"isStart":true})});
            var Q103;
            Q103=makeQuery(id+"F4.boolean.opBoolean","COPY",EDGE,{"derivedFrom":makeQuery(id+"F4.opExtrude","CAP_EDGE",EDGE,{"disambiguationData":[OSD([sQuery(id+"F3.wireOp",EDGE,"E7.1.0.6")])],"isStart":true})});
            var Q104;
            Q104=makeQuery(id+"F4.boolean.opBoolean","COPY",EDGE,{"derivedFrom":makeQuery(id+"F4.opExtrude","CAP_EDGE",EDGE,{"disambiguationData":[OSD([sQuery(id+"F3.wireOp",EDGE,"E7.1.0.5")])],"isStart":true})});
            var Q105;
            Q105=makeQuery(id+"F4.boolean.opBoolean","COPY",EDGE,{"derivedFrom":makeQuery(id+"F4.opExtrude","CAP_EDGE",EDGE,{"disambiguationData":[OSD([sQuery(id+"F3.wireOp",EDGE,"E7.1.0.1")])],"isStart":true})});
            var Q106;
            Q106=makeQuery(id+"F4.boolean.opBoolean","COPY",EDGE,{"derivedFrom":makeQuery(id+"F4.opExtrude","CAP_EDGE",EDGE,{"disambiguationData":[OSD([sQuery(id+"F3.wireOp",EDGE,"E7.1.0.3")])],"isStart":true})});
            var Q107;
            Q107=makeQuery(id+"F4.boolean.opBoolean","COPY",EDGE,{"derivedFrom":makeQuery(id+"F4.opExtrude","CAP_EDGE",EDGE,{"disambiguationData":[OSD([sQuery(id+"F3.wireOp",EDGE,"E7.2.0.2")])],"isStart":true})});
            var Q108;
            Q108=makeQuery(id+"F4.boolean.opBoolean","COPY",EDGE,{"derivedFrom":makeQuery(id+"F4.opExtrude","CAP_EDGE",EDGE,{"disambiguationData":[OSD([sQuery(id+"F3.wireOp",EDGE,"E7.2.0.5")])],"isStart":true})});
            var Q109;
            Q109=makeQuery(id+"F4.boolean.opBoolean","COPY",EDGE,{"derivedFrom":makeQuery(id+"F4.opExtrude","CAP_EDGE",EDGE,{"disambiguationData":[OSD([sQuery(id+"F3.wireOp",EDGE,"E7.2.0.0")])],"isStart":true})});
            var Q110;
            Q110=makeQuery(id+"F4.boolean.opBoolean","COPY",EDGE,{"derivedFrom":makeQuery(id+"F4.opExtrude","CAP_EDGE",EDGE,{"disambiguationData":[OSD([sQuery(id+"F3.wireOp",EDGE,"E7.2.0.6")])],"isStart":true})});
            var Q111;
            Q111=makeQuery(id+"F4.boolean.opBoolean","COPY",EDGE,{"derivedFrom":makeQuery(id+"F4.opExtrude","CAP_EDGE",EDGE,{"disambiguationData":[OSD([sQuery(id+"F3.wireOp",EDGE,"E7.2.0.3")])],"isStart":true})});
            var Q112;
            Q112=makeQuery(id+"F4.boolean.opBoolean","COPY",EDGE,{"derivedFrom":makeQuery(id+"F4.opExtrude","CAP_EDGE",EDGE,{"disambiguationData":[OSD([sQuery(id+"F3.wireOp",EDGE,"E7.2.0.1")])],"isStart":true})});
            var Q113;
            Q113=makeQuery(id+"F4.boolean.opBoolean","COPY",EDGE,{"derivedFrom":makeQuery(id+"F4.opExtrude","CAP_EDGE",EDGE,{"disambiguationData":[OSD([sQuery(id+"F3.wireOp",EDGE,"E7.2.0.5")])],"isStart":false})});
            var Q114;
            Q114=makeQuery(id+"F4.boolean.opBoolean","COPY",EDGE,{"derivedFrom":makeQuery(id+"F4.opExtrude","CAP_EDGE",EDGE,{"disambiguationData":[OSD([sQuery(id+"F3.wireOp",EDGE,"E7.2.0.2")])],"isStart":false})});
            var Q115;
            Q115=makeQuery(id+"F4.boolean.opBoolean","COPY",EDGE,{"derivedFrom":makeQuery(id+"F4.opExtrude","CAP_EDGE",EDGE,{"disambiguationData":[OSD([sQuery(id+"F3.wireOp",EDGE,"E7.1.0.0")])],"isStart":false})});
            var Q116;
            Q116=makeQuery(id+"F4.boolean.opBoolean","COPY",EDGE,{"derivedFrom":makeQuery(id+"F4.opExtrude","CAP_EDGE",EDGE,{"disambiguationData":[OSD([sQuery(id+"F3.wireOp",EDGE,"E7.1.0.2")])],"isStart":false})});
            var Q117;
            Q117=makeQuery(id+"F4.boolean.opBoolean","COPY",EDGE,{"derivedFrom":makeQuery(id+"F4.opExtrude","CAP_EDGE",EDGE,{"disambiguationData":[OSD([sQuery(id+"F3.wireOp",EDGE,"E7.1.0.5")])],"isStart":false})});
            var Q118;
            Q118=makeQuery(id+"F4.boolean.opBoolean","COPY",EDGE,{"derivedFrom":makeQuery(id+"F4.opExtrude","CAP_EDGE",EDGE,{"disambiguationData":[OSD([sQuery(id+"F3.wireOp",EDGE,"E7.1.0.1")])],"isStart":false})});
            var Q119;
            Q119=makeQuery(id+"F4.boolean.opBoolean","COPY",EDGE,{"derivedFrom":makeQuery(id+"F4.opExtrude","CAP_EDGE",EDGE,{"disambiguationData":[OSD([sQuery(id+"F3.wireOp",EDGE,"E7.1.0.3")])],"isStart":false})});
            var Q120;
            Q120=makeQuery(id+"F4.boolean.opBoolean","COPY",EDGE,{"derivedFrom":makeQuery(id+"F4.opExtrude","CAP_EDGE",EDGE,{"disambiguationData":[OSD([sQuery(id+"F3.wireOp",EDGE,"E7.1.0.6")])],"isStart":false})});
            var Q121;
            Q121=makeQuery(id+"F4.boolean.opBoolean","COPY",EDGE,{"derivedFrom":makeQuery(id+"F4.opExtrude","CAP_EDGE",EDGE,{"disambiguationData":[OSD([sQuery(id+"F3.wireOp",EDGE,"E7.2.0.6")])],"isStart":false})});
            var Q122;
            Q122=makeQuery(id+"F4.boolean.opBoolean","COPY",EDGE,{"derivedFrom":makeQuery(id+"F4.opExtrude","CAP_EDGE",EDGE,{"disambiguationData":[OSD([sQuery(id+"F3.wireOp",EDGE,"E7.3.0.2")])],"isStart":true})});
            var Q123;
            Q123=makeQuery(id+"F4.boolean.opBoolean","COPY",EDGE,{"derivedFrom":makeQuery(id+"F4.opExtrude","CAP_EDGE",EDGE,{"disambiguationData":[OSD([sQuery(id+"F3.wireOp",EDGE,"E7.3.0.2")])],"isStart":false})});
            var Q124;
            Q124=makeQuery(id+"F4.boolean.opBoolean","COPY",EDGE,{"derivedFrom":makeQuery(id+"F4.opExtrude","CAP_EDGE",EDGE,{"disambiguationData":[OSD([sQuery(id+"F3.wireOp",EDGE,"E7.3.0.0")])],"isStart":true})});
            var Q125;
            Q125=makeQuery(id+"F4.boolean.opBoolean","COPY",EDGE,{"derivedFrom":makeQuery(id+"F4.opExtrude","CAP_EDGE",EDGE,{"disambiguationData":[OSD([sQuery(id+"F3.wireOp",EDGE,"E7.3.0.0")])],"isStart":false})});
            var Q126;
            Q126=makeQuery(id+"F4.boolean.opBoolean","COPY",EDGE,{"derivedFrom":makeQuery(id+"F4.opExtrude","CAP_EDGE",EDGE,{"disambiguationData":[OSD([sQuery(id+"F3.wireOp",EDGE,"E7.3.0.6")])],"isStart":true})});
            var Q127;
            Q127=makeQuery(id+"F4.boolean.opBoolean","COPY",EDGE,{"derivedFrom":makeQuery(id+"F4.opExtrude","CAP_EDGE",EDGE,{"disambiguationData":[OSD([sQuery(id+"F3.wireOp",EDGE,"E7.3.0.6")])],"isStart":false})});
            var Q128;
            Q128=makeQuery(id+"F4.boolean.opBoolean","COPY",EDGE,{"derivedFrom":makeQuery(id+"F4.opExtrude","CAP_EDGE",EDGE,{"disambiguationData":[OSD([sQuery(id+"F3.wireOp",EDGE,"E7.3.0.3")])],"isStart":true})});
            var Q129;
            Q129=makeQuery(id+"F4.boolean.opBoolean","COPY",EDGE,{"derivedFrom":makeQuery(id+"F4.opExtrude","CAP_EDGE",EDGE,{"disambiguationData":[OSD([sQuery(id+"F3.wireOp",EDGE,"E7.3.0.3")])],"isStart":false})});
            var Q130;
            Q130=makeQuery(id+"F4.boolean.opBoolean","COPY",FACE,{"derivedFrom":makeQuery(id+"F4.opExtrude","CAP_FACE",FACE,{"disambiguationData":[OSD([sQuery(id+"F3.wireOp",EDGE,"E7.3.0.1")])],"isStart":false})});
            var Q131;
            Q131=makeQuery(id+"F4.boolean.opBoolean","COPY",EDGE,{"derivedFrom":makeQuery(id+"F4.opExtrude","CAP_EDGE",EDGE,{"disambiguationData":[OSD([sQuery(id+"F3.wireOp",EDGE,"E7.3.0.1")])],"isStart":true})});
            var Q132;
            Q132=makeQuery(id+"F4.boolean.opBoolean","COPY",FACE,{"derivedFrom":makeQuery(id+"F4.opExtrude","CAP_FACE",FACE,{"disambiguationData":[OSD([sQuery(id+"F3.wireOp",EDGE,"E7.3.0.5")])],"isStart":false})});
            var Q133;
            Q133=makeQuery(id+"F4.boolean.opBoolean","COPY",EDGE,{"derivedFrom":makeQuery(id+"F4.opExtrude","CAP_EDGE",EDGE,{"disambiguationData":[OSD([sQuery(id+"F3.wireOp",EDGE,"E7.3.0.5")])],"isStart":true})});
            var Q134;
            Q134=makeQuery(id+"F4.boolean.opBoolean","COPY",EDGE,{"derivedFrom":makeQuery(id+"F4.opExtrude","CAP_EDGE",EDGE,{"disambiguationData":[OSD([sQuery(id+"F3.wireOp",EDGE,"E7.4.0.2")])],"isStart":true})});
            var Q135;
            Q135=makeQuery(id+"F4.boolean.opBoolean","COPY",EDGE,{"derivedFrom":makeQuery(id+"F4.opExtrude","CAP_EDGE",EDGE,{"disambiguationData":[OSD([sQuery(id+"F3.wireOp",EDGE,"E7.4.0.0")])],"isStart":true})});
            var Q136;
            Q136=makeQuery(id+"F4.boolean.opBoolean","COPY",EDGE,{"derivedFrom":makeQuery(id+"F4.opExtrude","CAP_EDGE",EDGE,{"disambiguationData":[OSD([sQuery(id+"F3.wireOp",EDGE,"E7.4.0.6")])],"isStart":true})});
            var Q137;
            Q137=makeQuery(id+"F4.boolean.opBoolean","COPY",EDGE,{"derivedFrom":makeQuery(id+"F4.opExtrude","CAP_EDGE",EDGE,{"disambiguationData":[OSD([sQuery(id+"F3.wireOp",EDGE,"E7.4.0.3")])],"isStart":true})});
            var Q138;
            Q138=makeQuery(id+"F4.boolean.opBoolean","COPY",EDGE,{"derivedFrom":makeQuery(id+"F4.opExtrude","CAP_EDGE",EDGE,{"disambiguationData":[OSD([sQuery(id+"F3.wireOp",EDGE,"E7.4.0.1")])],"isStart":true})});
            var Q139;
            Q139=makeQuery(id+"F4.boolean.opBoolean","COPY",EDGE,{"derivedFrom":makeQuery(id+"F4.opExtrude","CAP_EDGE",EDGE,{"disambiguationData":[OSD([sQuery(id+"F3.wireOp",EDGE,"E7.4.0.5")])],"isStart":true})});
            var Q140;
            Q140=makeQuery(id+"F4.boolean.opBoolean","COPY",FACE,{"derivedFrom":makeQuery(id+"F4.opExtrude","CAP_FACE",FACE,{"disambiguationData":[OSD([sQuery(id+"F3.wireOp",EDGE,"E7.4.0.5")])],"isStart":false})});
            var Q141;
            Q141=makeQuery(id+"F4.boolean.opBoolean","COPY",FACE,{"derivedFrom":makeQuery(id+"F4.opExtrude","CAP_FACE",FACE,{"disambiguationData":[OSD([sQuery(id+"F3.wireOp",EDGE,"E7.4.0.2")])],"isStart":false})});
            var Q142;
            Q142=makeQuery(id+"F4.boolean.opBoolean","COPY",FACE,{"derivedFrom":makeQuery(id+"F4.opExtrude","CAP_FACE",FACE,{"disambiguationData":[OSD([sQuery(id+"F3.wireOp",EDGE,"E7.4.0.0")])],"isStart":false})});
            var Q143;
            Q143=makeQuery(id+"F4.boolean.opBoolean","COPY",FACE,{"derivedFrom":makeQuery(id+"F4.opExtrude","CAP_FACE",FACE,{"disambiguationData":[OSD([sQuery(id+"F3.wireOp",EDGE,"E7.4.0.6")])],"isStart":false})});
            var Q144;
            Q144=makeQuery(id+"F4.boolean.opBoolean","COPY",FACE,{"derivedFrom":makeQuery(id+"F4.opExtrude","CAP_FACE",FACE,{"disambiguationData":[OSD([sQuery(id+"F3.wireOp",EDGE,"E7.4.0.3")])],"isStart":false})});
            var Q145;
            Q145=makeQuery(id+"F4.boolean.opBoolean","COPY",FACE,{"derivedFrom":makeQuery(id+"F4.opExtrude","CAP_FACE",FACE,{"disambiguationData":[OSD([sQuery(id+"F3.wireOp",EDGE,"E7.4.0.1")])],"isStart":false})});
            var Q146;
            Q146=makeQuery(id+"F4.boolean.opBoolean","COPY",FACE,{"derivedFrom":makeQuery(id+"F4.opExtrude","CAP_FACE",FACE,{"disambiguationData":[OSD([sQuery(id+"F3.wireOp",EDGE,"E7.2.0.1")])],"isStart":false})});
            var Q147;
            Q147=makeQuery(id+"F4.boolean.opBoolean","COPY",FACE,{"derivedFrom":makeQuery(id+"F4.opExtrude","CAP_FACE",FACE,{"disambiguationData":[OSD([sQuery(id+"F3.wireOp",EDGE,"E7.2.0.3")])],"isStart":false})});
            var Q148;
            Q148=makeQuery(id+"F4.boolean.opBoolean","COPY",EDGE,{"derivedFrom":makeQuery(id+"F4.opExtrude","CAP_EDGE",EDGE,{"disambiguationData":[OSD([sQuery(id+"F3.wireOp",EDGE,"E7.0.1.0")])],"isStart":true})});
            var Q149;
            Q149=makeQuery(id+"F4.boolean.opBoolean","COPY",EDGE,{"derivedFrom":makeQuery(id+"F4.opExtrude","CAP_EDGE",EDGE,{"disambiguationData":[OSD([sQuery(id+"F3.wireOp",EDGE,"E7.0.1.2")])],"isStart":true})});
            var Q150;
            Q150=makeQuery(id+"F4.boolean.opBoolean","COPY",EDGE,{"derivedFrom":makeQuery(id+"F4.opExtrude","CAP_EDGE",EDGE,{"disambiguationData":[OSD([sQuery(id+"F3.wireOp",EDGE,"E7.0.1.5")])],"isStart":true})});
            var Q151;
            Q151=makeQuery(id+"F4.boolean.opBoolean","COPY",EDGE,{"derivedFrom":makeQuery(id+"F4.opExtrude","CAP_EDGE",EDGE,{"disambiguationData":[OSD([sQuery(id+"F3.wireOp",EDGE,"E7.0.1.6")])],"isStart":true})});
            var Q152;
            Q152=makeQuery(id+"F4.boolean.opBoolean","COPY",EDGE,{"derivedFrom":makeQuery(id+"F4.opExtrude","CAP_EDGE",EDGE,{"disambiguationData":[OSD([sQuery(id+"F3.wireOp",EDGE,"E7.0.1.3")])],"isStart":true})});
            var Q153;
            Q153=makeQuery(id+"F4.boolean.opBoolean","COPY",EDGE,{"derivedFrom":makeQuery(id+"F4.opExtrude","CAP_EDGE",EDGE,{"disambiguationData":[OSD([sQuery(id+"F3.wireOp",EDGE,"E7.0.1.1")])],"isStart":true})});
            var Q154;
            Q154=makeQuery(id+"F4.boolean.opBoolean","COPY",EDGE,{"derivedFrom":makeQuery(id+"F4.opExtrude","CAP_EDGE",EDGE,{"disambiguationData":[OSD([sQuery(id+"F3.wireOp",EDGE,"E7.1.1.0")])],"isStart":true})});
            var Q155;
            Q155=makeQuery(id+"F4.boolean.opBoolean","COPY",EDGE,{"derivedFrom":makeQuery(id+"F4.opExtrude","CAP_EDGE",EDGE,{"disambiguationData":[OSD([sQuery(id+"F3.wireOp",EDGE,"E7.1.1.2")])],"isStart":true})});
            var Q156;
            Q156=makeQuery(id+"F4.boolean.opBoolean","COPY",EDGE,{"derivedFrom":makeQuery(id+"F4.opExtrude","CAP_EDGE",EDGE,{"disambiguationData":[OSD([sQuery(id+"F3.wireOp",EDGE,"E7.1.1.5")])],"isStart":true})});
            var Q157;
            Q157=makeQuery(id+"F4.boolean.opBoolean","COPY",EDGE,{"derivedFrom":makeQuery(id+"F4.opExtrude","CAP_EDGE",EDGE,{"disambiguationData":[OSD([sQuery(id+"F3.wireOp",EDGE,"E7.1.1.1")])],"isStart":true})});
            var Q158;
            Q158=makeQuery(id+"F4.boolean.opBoolean","COPY",EDGE,{"derivedFrom":makeQuery(id+"F4.opExtrude","CAP_EDGE",EDGE,{"disambiguationData":[OSD([sQuery(id+"F3.wireOp",EDGE,"E7.1.1.3")])],"isStart":true})});
            var Q159;
            Q159=makeQuery(id+"F4.boolean.opBoolean","COPY",EDGE,{"derivedFrom":makeQuery(id+"F4.opExtrude","CAP_EDGE",EDGE,{"disambiguationData":[OSD([sQuery(id+"F3.wireOp",EDGE,"E7.1.1.6")])],"isStart":true})});
            var Q160;
            Q160=makeQuery(id+"F4.boolean.opBoolean","COPY",EDGE,{"derivedFrom":makeQuery(id+"F4.opExtrude","CAP_EDGE",EDGE,{"disambiguationData":[OSD([sQuery(id+"F3.wireOp",EDGE,"E7.2.1.2")])],"isStart":true})});
            var Q161;
            Q161=makeQuery(id+"F4.boolean.opBoolean","COPY",EDGE,{"derivedFrom":makeQuery(id+"F4.opExtrude","CAP_EDGE",EDGE,{"disambiguationData":[OSD([sQuery(id+"F3.wireOp",EDGE,"E7.2.1.0")])],"isStart":true})});
            var Q162;
            Q162=makeQuery(id+"F4.boolean.opBoolean","COPY",EDGE,{"derivedFrom":makeQuery(id+"F4.opExtrude","CAP_EDGE",EDGE,{"disambiguationData":[OSD([sQuery(id+"F3.wireOp",EDGE,"E7.2.1.6")])],"isStart":true})});
            var Q163;
            Q163=makeQuery(id+"F4.boolean.opBoolean","COPY",EDGE,{"derivedFrom":makeQuery(id+"F4.opExtrude","CAP_EDGE",EDGE,{"disambiguationData":[OSD([sQuery(id+"F3.wireOp",EDGE,"E7.2.1.3")])],"isStart":true})});
            var Q164;
            Q164=makeQuery(id+"F4.boolean.opBoolean","COPY",EDGE,{"derivedFrom":makeQuery(id+"F4.opExtrude","CAP_EDGE",EDGE,{"disambiguationData":[OSD([sQuery(id+"F3.wireOp",EDGE,"E7.2.1.1")])],"isStart":true})});
            var Q165;
            Q165=makeQuery(id+"F4.boolean.opBoolean","COPY",EDGE,{"derivedFrom":makeQuery(id+"F4.opExtrude","CAP_EDGE",EDGE,{"disambiguationData":[OSD([sQuery(id+"F3.wireOp",EDGE,"E7.2.1.5")])],"isStart":true})});
            var Q166;
            Q166=makeQuery(id+"F4.boolean.opBoolean","COPY",EDGE,{"derivedFrom":makeQuery(id+"F4.opExtrude","CAP_EDGE",EDGE,{"disambiguationData":[OSD([sQuery(id+"F3.wireOp",EDGE,"E7.3.1.2")])],"isStart":true})});
            var Q167;
            Q167=makeQuery(id+"F4.boolean.opBoolean","COPY",EDGE,{"derivedFrom":makeQuery(id+"F4.opExtrude","CAP_EDGE",EDGE,{"disambiguationData":[OSD([sQuery(id+"F3.wireOp",EDGE,"E7.3.1.0")])],"isStart":true})});
            var Q168;
            Q168=makeQuery(id+"F4.boolean.opBoolean","COPY",EDGE,{"derivedFrom":makeQuery(id+"F4.opExtrude","CAP_EDGE",EDGE,{"disambiguationData":[OSD([sQuery(id+"F3.wireOp",EDGE,"E7.3.1.6")])],"isStart":true})});
            var Q169;
            Q169=makeQuery(id+"F4.boolean.opBoolean","COPY",EDGE,{"derivedFrom":makeQuery(id+"F4.opExtrude","CAP_EDGE",EDGE,{"disambiguationData":[OSD([sQuery(id+"F3.wireOp",EDGE,"E7.3.1.3")])],"isStart":true})});
            var Q170;
            Q170=makeQuery(id+"F4.boolean.opBoolean","COPY",EDGE,{"derivedFrom":makeQuery(id+"F4.opExtrude","CAP_EDGE",EDGE,{"disambiguationData":[OSD([sQuery(id+"F3.wireOp",EDGE,"E7.3.1.1")])],"isStart":true})});
            var Q171;
            Q171=makeQuery(id+"F4.boolean.opBoolean","COPY",EDGE,{"derivedFrom":makeQuery(id+"F4.opExtrude","CAP_EDGE",EDGE,{"disambiguationData":[OSD([sQuery(id+"F3.wireOp",EDGE,"E7.3.1.5")])],"isStart":true})});
            var Q172;
            Q172=makeQuery(id+"F4.boolean.opBoolean","COPY",EDGE,{"derivedFrom":makeQuery(id+"F4.opExtrude","CAP_EDGE",EDGE,{"disambiguationData":[OSD([sQuery(id+"F3.wireOp",EDGE,"E7.4.1.5")])],"isStart":true})});
            var Q173;
            Q173=makeQuery(id+"F4.boolean.opBoolean","COPY",EDGE,{"derivedFrom":makeQuery(id+"F4.opExtrude","CAP_EDGE",EDGE,{"disambiguationData":[OSD([sQuery(id+"F3.wireOp",EDGE,"E7.4.1.2")])],"isStart":true})});
            var Q174;
            Q174=makeQuery(id+"F4.boolean.opBoolean","COPY",EDGE,{"derivedFrom":makeQuery(id+"F4.opExtrude","CAP_EDGE",EDGE,{"disambiguationData":[OSD([sQuery(id+"F3.wireOp",EDGE,"E7.4.1.0")])],"isStart":true})});
            var Q175;
            Q175=makeQuery(id+"F4.boolean.opBoolean","COPY",EDGE,{"derivedFrom":makeQuery(id+"F4.opExtrude","CAP_EDGE",EDGE,{"disambiguationData":[OSD([sQuery(id+"F3.wireOp",EDGE,"E7.4.1.6")])],"isStart":true})});
            var Q176;
            Q176=makeQuery(id+"F4.boolean.opBoolean","COPY",EDGE,{"derivedFrom":makeQuery(id+"F4.opExtrude","CAP_EDGE",EDGE,{"disambiguationData":[OSD([sQuery(id+"F3.wireOp",EDGE,"E7.4.1.1")])],"isStart":true})});
            var Q177;
            Q177=makeQuery(id+"F4.boolean.opBoolean","COPY",EDGE,{"derivedFrom":makeQuery(id+"F4.opExtrude","CAP_EDGE",EDGE,{"disambiguationData":[OSD([sQuery(id+"F3.wireOp",EDGE,"E7.4.1.3")])],"isStart":true})});
            var Q178;
            Q178=makeQuery(id+"F4.boolean.opBoolean","COPY",FACE,{"derivedFrom":makeQuery(id+"F4.opExtrude","CAP_FACE",FACE,{"disambiguationData":[OSD([sQuery(id+"F3.wireOp",EDGE,"E7.4.1.3")])],"isStart":false})});
            var Q179;
            Q179=makeQuery(id+"F4.boolean.opBoolean","COPY",FACE,{"derivedFrom":makeQuery(id+"F4.opExtrude","CAP_FACE",FACE,{"disambiguationData":[OSD([sQuery(id+"F3.wireOp",EDGE,"E7.4.1.6")])],"isStart":false})});
            var Q180;
            Q180=makeQuery(id+"F4.boolean.opBoolean","COPY",FACE,{"derivedFrom":makeQuery(id+"F4.opExtrude","CAP_FACE",FACE,{"disambiguationData":[OSD([sQuery(id+"F3.wireOp",EDGE,"E7.4.1.0")])],"isStart":false})});
            var Q181;
            Q181=makeQuery(id+"F4.boolean.opBoolean","COPY",FACE,{"derivedFrom":makeQuery(id+"F4.opExtrude","CAP_FACE",FACE,{"disambiguationData":[OSD([sQuery(id+"F3.wireOp",EDGE,"E7.4.1.2")])],"isStart":false})});
            var Q182;
            Q182=makeQuery(id+"F4.boolean.opBoolean","COPY",FACE,{"derivedFrom":makeQuery(id+"F4.opExtrude","CAP_FACE",FACE,{"disambiguationData":[OSD([sQuery(id+"F3.wireOp",EDGE,"E7.4.1.5")])],"isStart":false})});
            var Q183;
            Q183=makeQuery(id+"F4.boolean.opBoolean","COPY",FACE,{"derivedFrom":makeQuery(id+"F4.opExtrude","CAP_FACE",FACE,{"disambiguationData":[OSD([sQuery(id+"F3.wireOp",EDGE,"E7.4.1.1")])],"isStart":false})});
            var Q184;
            Q184=makeQuery(id+"F4.boolean.opBoolean","COPY",FACE,{"derivedFrom":makeQuery(id+"F4.opExtrude","CAP_FACE",FACE,{"disambiguationData":[OSD([sQuery(id+"F3.wireOp",EDGE,"E7.3.1.3")])],"isStart":false})});
            var Q185;
            Q185=makeQuery(id+"F4.boolean.opBoolean","COPY",FACE,{"derivedFrom":makeQuery(id+"F4.opExtrude","CAP_FACE",FACE,{"disambiguationData":[OSD([sQuery(id+"F3.wireOp",EDGE,"E7.3.1.6")])],"isStart":false})});
            var Q186;
            Q186=makeQuery(id+"F4.boolean.opBoolean","COPY",FACE,{"derivedFrom":makeQuery(id+"F4.opExtrude","CAP_FACE",FACE,{"disambiguationData":[OSD([sQuery(id+"F3.wireOp",EDGE,"E7.3.1.0")])],"isStart":false})});
            var Q187;
            Q187=makeQuery(id+"F4.boolean.opBoolean","COPY",FACE,{"derivedFrom":makeQuery(id+"F4.opExtrude","CAP_FACE",FACE,{"disambiguationData":[OSD([sQuery(id+"F3.wireOp",EDGE,"E7.3.1.5")])],"isStart":false})});
            var Q188;
            Q188=makeQuery(id+"F4.boolean.opBoolean","COPY",FACE,{"derivedFrom":makeQuery(id+"F4.opExtrude","CAP_FACE",FACE,{"disambiguationData":[OSD([sQuery(id+"F3.wireOp",EDGE,"E7.3.1.1")])],"isStart":false})});
            var Q189;
            Q189=makeQuery(id+"F4.boolean.opBoolean","COPY",FACE,{"derivedFrom":makeQuery(id+"F4.opExtrude","CAP_FACE",FACE,{"disambiguationData":[OSD([sQuery(id+"F3.wireOp",EDGE,"E7.2.1.3")])],"isStart":false})});
            var Q190;
            Q190=makeQuery(id+"F4.boolean.opBoolean","COPY",FACE,{"derivedFrom":makeQuery(id+"F4.opExtrude","CAP_FACE",FACE,{"disambiguationData":[OSD([sQuery(id+"F3.wireOp",EDGE,"E7.2.1.6")])],"isStart":false})});
            var Q191;
            Q191=makeQuery(id+"F4.boolean.opBoolean","COPY",FACE,{"derivedFrom":makeQuery(id+"F4.opExtrude","CAP_FACE",FACE,{"disambiguationData":[OSD([sQuery(id+"F3.wireOp",EDGE,"E7.2.1.0")])],"isStart":false})});
            var Q192;
            Q192=makeQuery(id+"F4.boolean.opBoolean","COPY",FACE,{"derivedFrom":makeQuery(id+"F4.opExtrude","CAP_FACE",FACE,{"disambiguationData":[OSD([sQuery(id+"F3.wireOp",EDGE,"E7.2.1.2")])],"isStart":false})});
            var Q193;
            Q193=makeQuery(id+"F4.boolean.opBoolean","COPY",FACE,{"derivedFrom":makeQuery(id+"F4.opExtrude","CAP_FACE",FACE,{"disambiguationData":[OSD([sQuery(id+"F3.wireOp",EDGE,"E7.2.1.5")])],"isStart":false})});
            var Q194;
            Q194=makeQuery(id+"F4.boolean.opBoolean","COPY",FACE,{"derivedFrom":makeQuery(id+"F4.opExtrude","CAP_FACE",FACE,{"disambiguationData":[OSD([sQuery(id+"F3.wireOp",EDGE,"E7.2.1.1")])],"isStart":false})});
            var Q195;
            Q195=makeQuery(id+"F4.boolean.opBoolean","COPY",FACE,{"derivedFrom":makeQuery(id+"F4.opExtrude","CAP_FACE",FACE,{"disambiguationData":[OSD([sQuery(id+"F3.wireOp",EDGE,"E7.1.1.3")])],"isStart":false})});
            var Q196;
            Q196=makeQuery(id+"F4.boolean.opBoolean","COPY",FACE,{"derivedFrom":makeQuery(id+"F4.opExtrude","CAP_FACE",FACE,{"disambiguationData":[OSD([sQuery(id+"F3.wireOp",EDGE,"E7.1.1.6")])],"isStart":false})});
            var Q197;
            Q197=makeQuery(id+"F4.boolean.opBoolean","COPY",FACE,{"derivedFrom":makeQuery(id+"F4.opExtrude","CAP_FACE",FACE,{"disambiguationData":[OSD([sQuery(id+"F3.wireOp",EDGE,"E7.1.1.0")])],"isStart":false})});
            var Q198;
            Q198=makeQuery(id+"F4.boolean.opBoolean","COPY",FACE,{"derivedFrom":makeQuery(id+"F4.opExtrude","CAP_FACE",FACE,{"disambiguationData":[OSD([sQuery(id+"F3.wireOp",EDGE,"E7.1.1.2")])],"isStart":false})});
            var Q199;
            Q199=makeQuery(id+"F4.boolean.opBoolean","COPY",FACE,{"derivedFrom":makeQuery(id+"F4.opExtrude","CAP_FACE",FACE,{"disambiguationData":[OSD([sQuery(id+"F3.wireOp",EDGE,"E7.1.1.5")])],"isStart":false})});
            var Q200;
            Q200=makeQuery(id+"F4.boolean.opBoolean","COPY",FACE,{"derivedFrom":makeQuery(id+"F4.opExtrude","CAP_FACE",FACE,{"disambiguationData":[OSD([sQuery(id+"F3.wireOp",EDGE,"E7.1.1.1")])],"isStart":false})});
            var Q201;
            Q201=makeQuery(id+"F4.boolean.opBoolean","COPY",FACE,{"derivedFrom":makeQuery(id+"F4.opExtrude","CAP_FACE",FACE,{"disambiguationData":[OSD([sQuery(id+"F3.wireOp",EDGE,"E7.0.1.0")])],"isStart":false})});
            var Q202;
            Q202=makeQuery(id+"F4.boolean.opBoolean","COPY",FACE,{"derivedFrom":makeQuery(id+"F4.opExtrude","CAP_FACE",FACE,{"disambiguationData":[OSD([sQuery(id+"F3.wireOp",EDGE,"E7.0.1.2")])],"isStart":false})});
            var Q203;
            Q203=makeQuery(id+"F4.boolean.opBoolean","COPY",FACE,{"derivedFrom":makeQuery(id+"F4.opExtrude","CAP_FACE",FACE,{"disambiguationData":[OSD([sQuery(id+"F3.wireOp",EDGE,"E7.0.1.5")])],"isStart":false})});
            var Q204;
            Q204=makeQuery(id+"F4.boolean.opBoolean","COPY",FACE,{"derivedFrom":makeQuery(id+"F4.opExtrude","CAP_FACE",FACE,{"disambiguationData":[OSD([sQuery(id+"F3.wireOp",EDGE,"E7.0.1.1")])],"isStart":false})});
            var Q205;
            Q205=makeQuery(id+"F4.boolean.opBoolean","COPY",FACE,{"derivedFrom":makeQuery(id+"F4.opExtrude","CAP_FACE",FACE,{"disambiguationData":[OSD([sQuery(id+"F3.wireOp",EDGE,"E7.0.1.3")])],"isStart":false})});
            var Q206;
            Q206=makeQuery(id+"F4.boolean.opBoolean","COPY",FACE,{"derivedFrom":makeQuery(id+"F4.opExtrude","CAP_FACE",FACE,{"disambiguationData":[OSD([sQuery(id+"F3.wireOp",EDGE,"E7.0.1.6")])],"isStart":false})});
            fillet(context, id + "F7", {"entities" : qUnion([Q0, Q1, Q2, Q3, Q4, Q5, Q6, Q7, Q8, Q9, Q10, Q11, Q12, Q13, Q14, Q15, Q16, Q17, Q18, Q19, Q20, Q21, Q22, Q23, Q24, Q25, Q26, Q27, Q28, Q29, Q30, Q31, Q32, Q33, Q34, Q35, Q36, Q37, Q38, Q39, Q40, Q41, Q42, Q43, Q44, Q45, Q46, Q47, Q48, Q49, Q50, Q51, Q52, Q53, Q54, Q55, Q56, Q57, Q58, Q59, Q60, Q61, Q62, Q63, Q64, Q65, Q66, Q67, Q68, Q69, Q70, Q71, Q72, Q73, Q74, Q75, Q76, Q77, Q78, Q79, Q80, Q81, Q82, Q83, Q84, Q85, Q86, Q87, Q88, Q89, Q90, Q91, Q92, Q93, Q94, Q95, Q96, Q97, Q98, Q99, Q100, Q101, Q102, Q103, Q104, Q105, Q106, Q107, Q108, Q109, Q110, Q111, Q112, Q113, Q114, Q115, Q116, Q117, Q118, Q119, Q120, Q121, Q122, Q123, Q124, Q125, Q126, Q127, Q128, Q129, Q130, Q131, Q132, Q133, Q134, Q135, Q136, Q137, Q138, Q139, Q140, Q141, Q142, Q143, Q144, Q145, Q146, Q147, Q148, Q149, Q150, Q151, Q152, Q153, Q154, Q155, Q156, Q157, Q158, Q159, Q160, Q161, Q162, Q163, Q164, Q165, Q166, Q167, Q168, Q169, Q170, Q171, Q172, Q173, Q174, Q175, Q176, Q177, Q178, Q179, Q180, Q181, Q182, Q183, Q184, Q185, Q186, Q187, Q188, Q189, Q190, Q191, Q192, Q193, Q194, Q195, Q196, Q197, Q198, Q199, Q200, Q201, Q202, Q203, Q204, Q205, Q206]), "radius" : 0.76 * mm, "tangentPropagation" : true, "allowEdgeOverflow" : false});
        }
        {
            var Q0;
            Q0=makeQuery(id+"F1.opExtrude","CAP_EDGE",EDGE,{"disambiguationData":[OSD([sQuery(id+"F0.wireOp",EDGE,"E0.top")])],"isStart":true});
            chamfer(context, id + "F8", {"entities" : qUnion([Q0]), "width" : 0.76 * mm, "tangentPropagation" : true});
        }
        {
            var Q0;
            Q0=makeQuery(id+"F1.opExtrude","SWEPT_FACE",FACE,{"disambiguationData":[OSD([sQuery(id+"F0.wireOp",EDGE,"E0.top")])]});
            var sketch = newSketch(context, id + "F9", { "sketchPlane" : qUnion([Q0])});
            skText(sketch, "E8", { "text": ".38 SPECIAL /.357 MAGNUM", "fontName": "OpenSans-Bold.ttf"});
            const initialGuessF9  = {"E8": [-0.08382, 0.00503, 1, 0, 0.00864]};
            skSetInitialGuess(sketch, initialGuessF9);
            skSolve(sketch);
        }
        {
            var Q0;
            Q0=qSketchRegion(id+"F9",true);
            extrude(context, id + "F10", {"entities" : qUnion([Q0]), "operationType" : NewBodyOperationType.ADD, "depth" : 0.5 * mm, "offsetDistance" : 25.4 * mm});
        }
        {
            var Q0;
            Q0=makeQuery(id+"F10.opExtrude","CAP_FACE",FACE,{"disambiguationData":[OSD([sQuery(id+"F9.wireOp",EDGE,"E8.sketch_text.stroke-0"),sQuery(id+"F9.wireOp",EDGE,"E8.sketch_text.stroke-1"),sQuery(id+"F9.wireOp",EDGE,"E8.sketch_text.stroke-2"),sQuery(id+"F9.wireOp",EDGE,"E8.sketch_text.stroke-3"),sQuery(id+"F9.wireOp",EDGE,"E8.sketch_text.stroke-4"),sQuery(id+"F9.wireOp",EDGE,"E8.sketch_text.stroke-5"),sQuery(id+"F9.wireOp",EDGE,"E8.sketch_text.stroke-6"),sQuery(id+"F9.wireOp",EDGE,"E8.sketch_text.stroke-7")])],"isStart":false});
            var Q1;
            Q1=makeQuery(id+"F10.opExtrude","CAP_FACE",FACE,{"disambiguationData":[OSD([sQuery(id+"F9.wireOp",EDGE,"E8.sketch_text.stroke-8"),sQuery(id+"F9.wireOp",EDGE,"E8.sketch_text.stroke-9"),sQuery(id+"F9.wireOp",EDGE,"E8.sketch_text.stroke-10"),sQuery(id+"F9.wireOp",EDGE,"E8.sketch_text.stroke-11"),sQuery(id+"F9.wireOp",EDGE,"E8.sketch_text.stroke-12"),sQuery(id+"F9.wireOp",EDGE,"E8.sketch_text.stroke-13"),sQuery(id+"F9.wireOp",EDGE,"E8.sketch_text.stroke-14"),sQuery(id+"F9.wireOp",EDGE,"E8.sketch_text.stroke-15"),sQuery(id+"F9.wireOp",EDGE,"E8.sketch_text.stroke-16"),sQuery(id+"F9.wireOp",EDGE,"E8.sketch_text.stroke-17"),sQuery(id+"F9.wireOp",EDGE,"E8.sketch_text.stroke-18"),sQuery(id+"F9.wireOp",EDGE,"E8.sketch_text.stroke-19"),sQuery(id+"F9.wireOp",EDGE,"E8.sketch_text.stroke-20"),sQuery(id+"F9.wireOp",EDGE,"E8.sketch_text.stroke-21"),sQuery(id+"F9.wireOp",EDGE,"E8.sketch_text.stroke-22"),sQuery(id+"F9.wireOp",EDGE,"E8.sketch_text.stroke-23"),sQuery(id+"F9.wireOp",EDGE,"E8.sketch_text.stroke-24"),sQuery(id+"F9.wireOp",EDGE,"E8.sketch_text.stroke-25"),sQuery(id+"F9.wireOp",EDGE,"E8.sketch_text.stroke-26"),sQuery(id+"F9.wireOp",EDGE,"E8.sketch_text.stroke-27"),sQuery(id+"F9.wireOp",EDGE,"E8.sketch_text.stroke-28"),sQuery(id+"F9.wireOp",EDGE,"E8.sketch_text.stroke-29"),sQuery(id+"F9.wireOp",EDGE,"E8.sketch_text.stroke-30"),sQuery(id+"F9.wireOp",EDGE,"E8.sketch_text.stroke-31"),sQuery(id+"F9.wireOp",EDGE,"E8.sketch_text.stroke-32"),sQuery(id+"F9.wireOp",EDGE,"E8.sketch_text.stroke-33"),sQuery(id+"F9.wireOp",EDGE,"E8.sketch_text.stroke-34")])],"isStart":false});
            var Q2;
            Q2=makeQuery(id+"F10.opExtrude","CAP_FACE",FACE,{"disambiguationData":[OSD([sQuery(id+"F9.wireOp",EDGE,"E8.sketch_text.stroke-35"),sQuery(id+"F9.wireOp",EDGE,"E8.sketch_text.stroke-36"),sQuery(id+"F9.wireOp",EDGE,"E8.sketch_text.stroke-37"),sQuery(id+"F9.wireOp",EDGE,"E8.sketch_text.stroke-38"),sQuery(id+"F9.wireOp",EDGE,"E8.sketch_text.stroke-39"),sQuery(id+"F9.wireOp",EDGE,"E8.sketch_text.stroke-40"),sQuery(id+"F9.wireOp",EDGE,"E8.sketch_text.stroke-41"),sQuery(id+"F9.wireOp",EDGE,"E8.sketch_text.stroke-42"),sQuery(id+"F9.wireOp",EDGE,"E8.sketch_text.stroke-43"),sQuery(id+"F9.wireOp",EDGE,"E8.sketch_text.stroke-44"),sQuery(id+"F9.wireOp",EDGE,"E8.sketch_text.stroke-45"),sQuery(id+"F9.wireOp",EDGE,"E8.sketch_text.stroke-46"),sQuery(id+"F9.wireOp",EDGE,"E8.sketch_text.stroke-47"),sQuery(id+"F9.wireOp",EDGE,"E8.sketch_text.stroke-48"),sQuery(id+"F9.wireOp",EDGE,"E8.sketch_text.stroke-49"),sQuery(id+"F9.wireOp",EDGE,"E8.sketch_text.stroke-50"),sQuery(id+"F9.wireOp",EDGE,"E8.sketch_text.stroke-51"),sQuery(id+"F9.wireOp",EDGE,"E8.sketch_text.stroke-52"),sQuery(id+"F9.wireOp",EDGE,"E8.sketch_text.stroke-53"),sQuery(id+"F9.wireOp",EDGE,"E8.sketch_text.stroke-54"),sQuery(id+"F9.wireOp",EDGE,"E8.sketch_text.stroke-55"),sQuery(id+"F9.wireOp",EDGE,"E8.sketch_text.stroke-56"),sQuery(id+"F9.wireOp",EDGE,"E8.sketch_text.stroke-57"),sQuery(id+"F9.wireOp",EDGE,"E8.sketch_text.stroke-58"),sQuery(id+"F9.wireOp",EDGE,"E8.sketch_text.stroke-59"),sQuery(id+"F9.wireOp",EDGE,"E8.sketch_text.stroke-60"),sQuery(id+"F9.wireOp",EDGE,"E8.sketch_text.stroke-61"),sQuery(id+"F9.wireOp",EDGE,"E8.sketch_text.stroke-62"),sQuery(id+"F9.wireOp",EDGE,"E8.sketch_text.stroke-63"),sQuery(id+"F9.wireOp",EDGE,"E8.sketch_text.stroke-64"),sQuery(id+"F9.wireOp",EDGE,"E8.sketch_text.stroke-65")])],"isStart":false});
            var Q3;
            Q3=makeQuery(id+"F10.opExtrude","CAP_FACE",FACE,{"disambiguationData":[OSD([sQuery(id+"F9.wireOp",EDGE,"E8.sketch_text.stroke-66"),sQuery(id+"F9.wireOp",EDGE,"E8.sketch_text.stroke-67"),sQuery(id+"F9.wireOp",EDGE,"E8.sketch_text.stroke-68"),sQuery(id+"F9.wireOp",EDGE,"E8.sketch_text.stroke-69"),sQuery(id+"F9.wireOp",EDGE,"E8.sketch_text.stroke-70"),sQuery(id+"F9.wireOp",EDGE,"E8.sketch_text.stroke-71"),sQuery(id+"F9.wireOp",EDGE,"E8.sketch_text.stroke-72"),sQuery(id+"F9.wireOp",EDGE,"E8.sketch_text.stroke-73"),sQuery(id+"F9.wireOp",EDGE,"E8.sketch_text.stroke-74"),sQuery(id+"F9.wireOp",EDGE,"E8.sketch_text.stroke-75"),sQuery(id+"F9.wireOp",EDGE,"E8.sketch_text.stroke-76"),sQuery(id+"F9.wireOp",EDGE,"E8.sketch_text.stroke-77"),sQuery(id+"F9.wireOp",EDGE,"E8.sketch_text.stroke-78"),sQuery(id+"F9.wireOp",EDGE,"E8.sketch_text.stroke-79"),sQuery(id+"F9.wireOp",EDGE,"E8.sketch_text.stroke-80"),sQuery(id+"F9.wireOp",EDGE,"E8.sketch_text.stroke-81"),sQuery(id+"F9.wireOp",EDGE,"E8.sketch_text.stroke-82"),sQuery(id+"F9.wireOp",EDGE,"E8.sketch_text.stroke-83"),sQuery(id+"F9.wireOp",EDGE,"E8.sketch_text.stroke-84"),sQuery(id+"F9.wireOp",EDGE,"E8.sketch_text.stroke-85"),sQuery(id+"F9.wireOp",EDGE,"E8.sketch_text.stroke-86"),sQuery(id+"F9.wireOp",EDGE,"E8.sketch_text.stroke-87"),sQuery(id+"F9.wireOp",EDGE,"E8.sketch_text.stroke-88"),sQuery(id+"F9.wireOp",EDGE,"E8.sketch_text.stroke-89"),sQuery(id+"F9.wireOp",EDGE,"E8.sketch_text.stroke-90"),sQuery(id+"F9.wireOp",EDGE,"E8.sketch_text.stroke-91"),sQuery(id+"F9.wireOp",EDGE,"E8.sketch_text.stroke-92"),sQuery(id+"F9.wireOp",EDGE,"E8.sketch_text.stroke-93")])],"isStart":false});
            var Q4;
            Q4=makeQuery(id+"F10.opExtrude","CAP_FACE",FACE,{"disambiguationData":[OSD([sQuery(id+"F9.wireOp",EDGE,"E8.sketch_text.stroke-94"),sQuery(id+"F9.wireOp",EDGE,"E8.sketch_text.stroke-95"),sQuery(id+"F9.wireOp",EDGE,"E8.sketch_text.stroke-96"),sQuery(id+"F9.wireOp",EDGE,"E8.sketch_text.stroke-97"),sQuery(id+"F9.wireOp",EDGE,"E8.sketch_text.stroke-98"),sQuery(id+"F9.wireOp",EDGE,"E8.sketch_text.stroke-99"),sQuery(id+"F9.wireOp",EDGE,"E8.sketch_text.stroke-100"),sQuery(id+"F9.wireOp",EDGE,"E8.sketch_text.stroke-101"),sQuery(id+"F9.wireOp",EDGE,"E8.sketch_text.stroke-102"),sQuery(id+"F9.wireOp",EDGE,"E8.sketch_text.stroke-103"),sQuery(id+"F9.wireOp",EDGE,"E8.sketch_text.stroke-104"),sQuery(id+"F9.wireOp",EDGE,"E8.sketch_text.stroke-105"),sQuery(id+"F9.wireOp",EDGE,"E8.sketch_text.stroke-106"),sQuery(id+"F9.wireOp",EDGE,"E8.sketch_text.stroke-107"),sQuery(id+"F9.wireOp",EDGE,"E8.sketch_text.stroke-108"),sQuery(id+"F9.wireOp",EDGE,"E8.sketch_text.stroke-109")])],"isStart":false});
            var Q5;
            Q5=makeQuery(id+"F10.opExtrude","CAP_FACE",FACE,{"disambiguationData":[OSD([sQuery(id+"F9.wireOp",EDGE,"E8.sketch_text.stroke-110"),sQuery(id+"F9.wireOp",EDGE,"E8.sketch_text.stroke-111"),sQuery(id+"F9.wireOp",EDGE,"E8.sketch_text.stroke-112"),sQuery(id+"F9.wireOp",EDGE,"E8.sketch_text.stroke-113"),sQuery(id+"F9.wireOp",EDGE,"E8.sketch_text.stroke-114"),sQuery(id+"F9.wireOp",EDGE,"E8.sketch_text.stroke-115"),sQuery(id+"F9.wireOp",EDGE,"E8.sketch_text.stroke-116"),sQuery(id+"F9.wireOp",EDGE,"E8.sketch_text.stroke-117"),sQuery(id+"F9.wireOp",EDGE,"E8.sketch_text.stroke-118"),sQuery(id+"F9.wireOp",EDGE,"E8.sketch_text.stroke-119"),sQuery(id+"F9.wireOp",EDGE,"E8.sketch_text.stroke-120"),sQuery(id+"F9.wireOp",EDGE,"E8.sketch_text.stroke-121")])],"isStart":false});
            var Q6;
            Q6=makeQuery(id+"F10.opExtrude","CAP_FACE",FACE,{"disambiguationData":[OSD([sQuery(id+"F9.wireOp",EDGE,"E8.sketch_text.stroke-137"),sQuery(id+"F9.wireOp",EDGE,"E8.sketch_text.stroke-138"),sQuery(id+"F9.wireOp",EDGE,"E8.sketch_text.stroke-139"),sQuery(id+"F9.wireOp",EDGE,"E8.sketch_text.stroke-140")])],"isStart":false});
            var Q7;
            Q7=makeQuery(id+"F10.opExtrude","CAP_FACE",FACE,{"disambiguationData":[OSD([sQuery(id+"F9.wireOp",EDGE,"E8.sketch_text.stroke-122"),sQuery(id+"F9.wireOp",EDGE,"E8.sketch_text.stroke-123"),sQuery(id+"F9.wireOp",EDGE,"E8.sketch_text.stroke-124"),sQuery(id+"F9.wireOp",EDGE,"E8.sketch_text.stroke-125"),sQuery(id+"F9.wireOp",EDGE,"E8.sketch_text.stroke-126"),sQuery(id+"F9.wireOp",EDGE,"E8.sketch_text.stroke-127"),sQuery(id+"F9.wireOp",EDGE,"E8.sketch_text.stroke-128"),sQuery(id+"F9.wireOp",EDGE,"E8.sketch_text.stroke-129"),sQuery(id+"F9.wireOp",EDGE,"E8.sketch_text.stroke-130"),sQuery(id+"F9.wireOp",EDGE,"E8.sketch_text.stroke-131"),sQuery(id+"F9.wireOp",EDGE,"E8.sketch_text.stroke-132"),sQuery(id+"F9.wireOp",EDGE,"E8.sketch_text.stroke-133"),sQuery(id+"F9.wireOp",EDGE,"E8.sketch_text.stroke-134"),sQuery(id+"F9.wireOp",EDGE,"E8.sketch_text.stroke-135"),sQuery(id+"F9.wireOp",EDGE,"E8.sketch_text.stroke-136")])],"isStart":false});
            fillet(context, id + "F11", {"entities" : qUnion([Q0, Q1, Q2, Q3, Q4, Q5, Q6, Q7]), "radius" : 0.25 * mm, "tangentPropagation" : true, "allowEdgeOverflow" : false});
        }
        {
            var Q0;
            Q0=makeQuery(id+"F10.opExtrude","CAP_EDGE",EDGE,{"disambiguationData":[OSD([sQuery(id+"F9.wireOp",EDGE,"E8.sketch_text.stroke-145")])],"isStart":false});
            var Q1;
            Q1=makeQuery(id+"F10.opExtrude","CAP_EDGE",EDGE,{"disambiguationData":[OSD([sQuery(id+"F9.wireOp",EDGE,"E8.sketch_text.stroke-146")])],"isStart":false});
            var Q2;
            Q2=makeQuery(id+"F10.opExtrude","CAP_EDGE",EDGE,{"disambiguationData":[OSD([sQuery(id+"F9.wireOp",EDGE,"E8.sketch_text.stroke-147")])],"isStart":false});
            var Q3;
            Q3=makeQuery(id+"F10.opExtrude","CAP_EDGE",EDGE,{"disambiguationData":[OSD([sQuery(id+"F9.wireOp",EDGE,"E8.sketch_text.stroke-148")])],"isStart":false});
            var Q4;
            Q4=makeQuery(id+"F10.opExtrude","CAP_EDGE",EDGE,{"disambiguationData":[OSD([sQuery(id+"F9.wireOp",EDGE,"E8.sketch_text.stroke-141")])],"isStart":false});
            var Q5;
            Q5=makeQuery(id+"F10.opExtrude","CAP_EDGE",EDGE,{"disambiguationData":[OSD([sQuery(id+"F9.wireOp",EDGE,"E8.sketch_text.stroke-142")])],"isStart":false});
            var Q6;
            Q6=makeQuery(id+"F10.opExtrude","CAP_EDGE",EDGE,{"disambiguationData":[OSD([sQuery(id+"F9.wireOp",EDGE,"E8.sketch_text.stroke-143")])],"isStart":false});
            var Q7;
            Q7=makeQuery(id+"F10.opExtrude","CAP_EDGE",EDGE,{"disambiguationData":[OSD([sQuery(id+"F9.wireOp",EDGE,"E8.sketch_text.stroke-144")])],"isStart":false});
            var Q8;
            Q8=makeQuery(id+"F10.opExtrude","CAP_FACE",FACE,{"disambiguationData":[OSD([sQuery(id+"F9.wireOp",EDGE,"E8.sketch_text.stroke-153"),sQuery(id+"F9.wireOp",EDGE,"E8.sketch_text.stroke-154"),sQuery(id+"F9.wireOp",EDGE,"E8.sketch_text.stroke-155"),sQuery(id+"F9.wireOp",EDGE,"E8.sketch_text.stroke-156"),sQuery(id+"F9.wireOp",EDGE,"E8.sketch_text.stroke-157"),sQuery(id+"F9.wireOp",EDGE,"E8.sketch_text.stroke-158")])],"isStart":false});
            var Q9;
            Q9=makeQuery(id+"F10.opExtrude","CAP_FACE",FACE,{"disambiguationData":[OSD([sQuery(id+"F9.wireOp",EDGE,"E8.sketch_text.stroke-159"),sQuery(id+"F9.wireOp",EDGE,"E8.sketch_text.stroke-160"),sQuery(id+"F9.wireOp",EDGE,"E8.sketch_text.stroke-161"),sQuery(id+"F9.wireOp",EDGE,"E8.sketch_text.stroke-162")])],"isStart":false});
            var Q10;
            Q10=makeQuery(id+"F10.opExtrude","CAP_FACE",FACE,{"disambiguationData":[OSD([sQuery(id+"F9.wireOp",EDGE,"E8.sketch_text.stroke-163"),sQuery(id+"F9.wireOp",EDGE,"E8.sketch_text.stroke-164"),sQuery(id+"F9.wireOp",EDGE,"E8.sketch_text.stroke-165"),sQuery(id+"F9.wireOp",EDGE,"E8.sketch_text.stroke-166"),sQuery(id+"F9.wireOp",EDGE,"E8.sketch_text.stroke-167"),sQuery(id+"F9.wireOp",EDGE,"E8.sketch_text.stroke-168"),sQuery(id+"F9.wireOp",EDGE,"E8.sketch_text.stroke-169"),sQuery(id+"F9.wireOp",EDGE,"E8.sketch_text.stroke-170")])],"isStart":false});
            var Q11;
            Q11=makeQuery(id+"F10.opExtrude","CAP_FACE",FACE,{"disambiguationData":[OSD([sQuery(id+"F9.wireOp",EDGE,"E8.sketch_text.stroke-171"),sQuery(id+"F9.wireOp",EDGE,"E8.sketch_text.stroke-172"),sQuery(id+"F9.wireOp",EDGE,"E8.sketch_text.stroke-173"),sQuery(id+"F9.wireOp",EDGE,"E8.sketch_text.stroke-174"),sQuery(id+"F9.wireOp",EDGE,"E8.sketch_text.stroke-175"),sQuery(id+"F9.wireOp",EDGE,"E8.sketch_text.stroke-176"),sQuery(id+"F9.wireOp",EDGE,"E8.sketch_text.stroke-177"),sQuery(id+"F9.wireOp",EDGE,"E8.sketch_text.stroke-178"),sQuery(id+"F9.wireOp",EDGE,"E8.sketch_text.stroke-179"),sQuery(id+"F9.wireOp",EDGE,"E8.sketch_text.stroke-180"),sQuery(id+"F9.wireOp",EDGE,"E8.sketch_text.stroke-181"),sQuery(id+"F9.wireOp",EDGE,"E8.sketch_text.stroke-182"),sQuery(id+"F9.wireOp",EDGE,"E8.sketch_text.stroke-183"),sQuery(id+"F9.wireOp",EDGE,"E8.sketch_text.stroke-184"),sQuery(id+"F9.wireOp",EDGE,"E8.sketch_text.stroke-185"),sQuery(id+"F9.wireOp",EDGE,"E8.sketch_text.stroke-186"),sQuery(id+"F9.wireOp",EDGE,"E8.sketch_text.stroke-187"),sQuery(id+"F9.wireOp",EDGE,"E8.sketch_text.stroke-188"),sQuery(id+"F9.wireOp",EDGE,"E8.sketch_text.stroke-189"),sQuery(id+"F9.wireOp",EDGE,"E8.sketch_text.stroke-190"),sQuery(id+"F9.wireOp",EDGE,"E8.sketch_text.stroke-191"),sQuery(id+"F9.wireOp",EDGE,"E8.sketch_text.stroke-192"),sQuery(id+"F9.wireOp",EDGE,"E8.sketch_text.stroke-193"),sQuery(id+"F9.wireOp",EDGE,"E8.sketch_text.stroke-194"),sQuery(id+"F9.wireOp",EDGE,"E8.sketch_text.stroke-195"),sQuery(id+"F9.wireOp",EDGE,"E8.sketch_text.stroke-196"),sQuery(id+"F9.wireOp",EDGE,"E8.sketch_text.stroke-197")])],"isStart":false});
            var Q12;
            Q12=makeQuery(id+"F10.opExtrude","CAP_FACE",FACE,{"disambiguationData":[OSD([sQuery(id+"F9.wireOp",EDGE,"E8.sketch_text.stroke-198"),sQuery(id+"F9.wireOp",EDGE,"E8.sketch_text.stroke-199"),sQuery(id+"F9.wireOp",EDGE,"E8.sketch_text.stroke-200"),sQuery(id+"F9.wireOp",EDGE,"E8.sketch_text.stroke-201"),sQuery(id+"F9.wireOp",EDGE,"E8.sketch_text.stroke-202"),sQuery(id+"F9.wireOp",EDGE,"E8.sketch_text.stroke-203"),sQuery(id+"F9.wireOp",EDGE,"E8.sketch_text.stroke-204"),sQuery(id+"F9.wireOp",EDGE,"E8.sketch_text.stroke-205"),sQuery(id+"F9.wireOp",EDGE,"E8.sketch_text.stroke-206"),sQuery(id+"F9.wireOp",EDGE,"E8.sketch_text.stroke-207"),sQuery(id+"F9.wireOp",EDGE,"E8.sketch_text.stroke-208"),sQuery(id+"F9.wireOp",EDGE,"E8.sketch_text.stroke-209"),sQuery(id+"F9.wireOp",EDGE,"E8.sketch_text.stroke-210"),sQuery(id+"F9.wireOp",EDGE,"E8.sketch_text.stroke-211"),sQuery(id+"F9.wireOp",EDGE,"E8.sketch_text.stroke-212"),sQuery(id+"F9.wireOp",EDGE,"E8.sketch_text.stroke-213"),sQuery(id+"F9.wireOp",EDGE,"E8.sketch_text.stroke-214"),sQuery(id+"F9.wireOp",EDGE,"E8.sketch_text.stroke-215"),sQuery(id+"F9.wireOp",EDGE,"E8.sketch_text.stroke-216"),sQuery(id+"F9.wireOp",EDGE,"E8.sketch_text.stroke-217")])],"isStart":false});
            var Q13;
            Q13=makeQuery(id+"F10.opExtrude","CAP_FACE",FACE,{"disambiguationData":[OSD([sQuery(id+"F9.wireOp",EDGE,"E8.sketch_text.stroke-218"),sQuery(id+"F9.wireOp",EDGE,"E8.sketch_text.stroke-219"),sQuery(id+"F9.wireOp",EDGE,"E8.sketch_text.stroke-220"),sQuery(id+"F9.wireOp",EDGE,"E8.sketch_text.stroke-221"),sQuery(id+"F9.wireOp",EDGE,"E8.sketch_text.stroke-222"),sQuery(id+"F9.wireOp",EDGE,"E8.sketch_text.stroke-223"),sQuery(id+"F9.wireOp",EDGE,"E8.sketch_text.stroke-224")])],"isStart":false});
            var Q14;
            Q14=makeQuery(id+"F10.opExtrude","CAP_FACE",FACE,{"disambiguationData":[OSD([sQuery(id+"F9.wireOp",EDGE,"E8.sketch_text.stroke-225"),sQuery(id+"F9.wireOp",EDGE,"E8.sketch_text.stroke-226"),sQuery(id+"F9.wireOp",EDGE,"E8.sketch_text.stroke-227"),sQuery(id+"F9.wireOp",EDGE,"E8.sketch_text.stroke-228"),sQuery(id+"F9.wireOp",EDGE,"E8.sketch_text.stroke-229"),sQuery(id+"F9.wireOp",EDGE,"E8.sketch_text.stroke-230"),sQuery(id+"F9.wireOp",EDGE,"E8.sketch_text.stroke-231"),sQuery(id+"F9.wireOp",EDGE,"E8.sketch_text.stroke-232"),sQuery(id+"F9.wireOp",EDGE,"E8.sketch_text.stroke-233"),sQuery(id+"F9.wireOp",EDGE,"E8.sketch_text.stroke-234"),sQuery(id+"F9.wireOp",EDGE,"E8.sketch_text.stroke-235"),sQuery(id+"F9.wireOp",EDGE,"E8.sketch_text.stroke-236"),sQuery(id+"F9.wireOp",EDGE,"E8.sketch_text.stroke-237"),sQuery(id+"F9.wireOp",EDGE,"E8.sketch_text.stroke-238"),sQuery(id+"F9.wireOp",EDGE,"E8.sketch_text.stroke-239"),sQuery(id+"F9.wireOp",EDGE,"E8.sketch_text.stroke-240"),sQuery(id+"F9.wireOp",EDGE,"E8.sketch_text.stroke-241"),sQuery(id+"F9.wireOp",EDGE,"E8.sketch_text.stroke-242"),sQuery(id+"F9.wireOp",EDGE,"E8.sketch_text.stroke-243")])],"isStart":false});
            var Q15;
            Q15=makeQuery(id+"F10.opExtrude","CAP_FACE",FACE,{"disambiguationData":[OSD([sQuery(id+"F9.wireOp",EDGE,"E8.sketch_text.stroke-256"),sQuery(id+"F9.wireOp",EDGE,"E8.sketch_text.stroke-257"),sQuery(id+"F9.wireOp",EDGE,"E8.sketch_text.stroke-258"),sQuery(id+"F9.wireOp",EDGE,"E8.sketch_text.stroke-259"),sQuery(id+"F9.wireOp",EDGE,"E8.sketch_text.stroke-260"),sQuery(id+"F9.wireOp",EDGE,"E8.sketch_text.stroke-261"),sQuery(id+"F9.wireOp",EDGE,"E8.sketch_text.stroke-262"),sQuery(id+"F9.wireOp",EDGE,"E8.sketch_text.stroke-263"),sQuery(id+"F9.wireOp",EDGE,"E8.sketch_text.stroke-264"),sQuery(id+"F9.wireOp",EDGE,"E8.sketch_text.stroke-265"),sQuery(id+"F9.wireOp",EDGE,"E8.sketch_text.stroke-266"),sQuery(id+"F9.wireOp",EDGE,"E8.sketch_text.stroke-267"),sQuery(id+"F9.wireOp",EDGE,"E8.sketch_text.stroke-268"),sQuery(id+"F9.wireOp",EDGE,"E8.sketch_text.stroke-269"),sQuery(id+"F9.wireOp",EDGE,"E8.sketch_text.stroke-270"),sQuery(id+"F9.wireOp",EDGE,"E8.sketch_text.stroke-271"),sQuery(id+"F9.wireOp",EDGE,"E8.sketch_text.stroke-272"),sQuery(id+"F9.wireOp",EDGE,"E8.sketch_text.stroke-273"),sQuery(id+"F9.wireOp",EDGE,"E8.sketch_text.stroke-274")])],"isStart":false});
            var Q16;
            Q16=makeQuery(id+"F10.opExtrude","CAP_FACE",FACE,{"disambiguationData":[OSD([sQuery(id+"F9.wireOp",EDGE,"E8.sketch_text.stroke-275"),sQuery(id+"F9.wireOp",EDGE,"E8.sketch_text.stroke-276"),sQuery(id+"F9.wireOp",EDGE,"E8.sketch_text.stroke-277"),sQuery(id+"F9.wireOp",EDGE,"E8.sketch_text.stroke-278"),sQuery(id+"F9.wireOp",EDGE,"E8.sketch_text.stroke-279"),sQuery(id+"F9.wireOp",EDGE,"E8.sketch_text.stroke-280"),sQuery(id+"F9.wireOp",EDGE,"E8.sketch_text.stroke-281"),sQuery(id+"F9.wireOp",EDGE,"E8.sketch_text.stroke-282"),sQuery(id+"F9.wireOp",EDGE,"E8.sketch_text.stroke-283"),sQuery(id+"F9.wireOp",EDGE,"E8.sketch_text.stroke-284"),sQuery(id+"F9.wireOp",EDGE,"E8.sketch_text.stroke-285"),sQuery(id+"F9.wireOp",EDGE,"E8.sketch_text.stroke-286"),sQuery(id+"F9.wireOp",EDGE,"E8.sketch_text.stroke-287"),sQuery(id+"F9.wireOp",EDGE,"E8.sketch_text.stroke-288")])],"isStart":false});
            var Q17;
            Q17=makeQuery(id+"F10.opExtrude","CAP_FACE",FACE,{"disambiguationData":[OSD([sQuery(id+"F9.wireOp",EDGE,"E8.sketch_text.stroke-289"),sQuery(id+"F9.wireOp",EDGE,"E8.sketch_text.stroke-290"),sQuery(id+"F9.wireOp",EDGE,"E8.sketch_text.stroke-291"),sQuery(id+"F9.wireOp",EDGE,"E8.sketch_text.stroke-292"),sQuery(id+"F9.wireOp",EDGE,"E8.sketch_text.stroke-293"),sQuery(id+"F9.wireOp",EDGE,"E8.sketch_text.stroke-294"),sQuery(id+"F9.wireOp",EDGE,"E8.sketch_text.stroke-295"),sQuery(id+"F9.wireOp",EDGE,"E8.sketch_text.stroke-296"),sQuery(id+"F9.wireOp",EDGE,"E8.sketch_text.stroke-297"),sQuery(id+"F9.wireOp",EDGE,"E8.sketch_text.stroke-298"),sQuery(id+"F9.wireOp",EDGE,"E8.sketch_text.stroke-299"),sQuery(id+"F9.wireOp",EDGE,"E8.sketch_text.stroke-300"),sQuery(id+"F9.wireOp",EDGE,"E8.sketch_text.stroke-301"),sQuery(id+"F9.wireOp",EDGE,"E8.sketch_text.stroke-302"),sQuery(id+"F9.wireOp",EDGE,"E8.sketch_text.stroke-303")])],"isStart":false});
            var Q18;
            Q18=makeQuery(id+"F10.opExtrude","CAP_FACE",FACE,{"disambiguationData":[OSD([sQuery(id+"F9.wireOp",EDGE,"E8.sketch_text.stroke-304"),sQuery(id+"F9.wireOp",EDGE,"E8.sketch_text.stroke-305"),sQuery(id+"F9.wireOp",EDGE,"E8.sketch_text.stroke-306"),sQuery(id+"F9.wireOp",EDGE,"E8.sketch_text.stroke-307"),sQuery(id+"F9.wireOp",EDGE,"E8.sketch_text.stroke-308"),sQuery(id+"F9.wireOp",EDGE,"E8.sketch_text.stroke-309"),sQuery(id+"F9.wireOp",EDGE,"E8.sketch_text.stroke-310"),sQuery(id+"F9.wireOp",EDGE,"E8.sketch_text.stroke-311"),sQuery(id+"F9.wireOp",EDGE,"E8.sketch_text.stroke-312"),sQuery(id+"F9.wireOp",EDGE,"E8.sketch_text.stroke-313"),sQuery(id+"F9.wireOp",EDGE,"E8.sketch_text.stroke-314"),sQuery(id+"F9.wireOp",EDGE,"E8.sketch_text.stroke-315"),sQuery(id+"F9.wireOp",EDGE,"E8.sketch_text.stroke-316"),sQuery(id+"F9.wireOp",EDGE,"E8.sketch_text.stroke-317"),sQuery(id+"F9.wireOp",EDGE,"E8.sketch_text.stroke-318"),sQuery(id+"F9.wireOp",EDGE,"E8.sketch_text.stroke-319"),sQuery(id+"F9.wireOp",EDGE,"E8.sketch_text.stroke-320"),sQuery(id+"F9.wireOp",EDGE,"E8.sketch_text.stroke-321"),sQuery(id+"F9.wireOp",EDGE,"E8.sketch_text.stroke-322")])],"isStart":false});
            var Q19;
            Q19=makeQuery(id+"F10.opExtrude","CAP_EDGE",EDGE,{"disambiguationData":[OSD([sQuery(id+"F9.wireOp",EDGE,"E8.sketch_text.stroke-245")])],"isStart":false});
            var Q20;
            Q20=makeQuery(id+"F10.opExtrude","CAP_EDGE",EDGE,{"disambiguationData":[OSD([sQuery(id+"F9.wireOp",EDGE,"E8.sketch_text.stroke-244")])],"isStart":false});
            var Q21;
            Q21=makeQuery(id+"F10.opExtrude","CAP_EDGE",EDGE,{"disambiguationData":[OSD([sQuery(id+"F9.wireOp",EDGE,"E8.sketch_text.stroke-251")])],"isStart":false});
            var Q22;
            Q22=makeQuery(id+"F10.opExtrude","CAP_EDGE",EDGE,{"disambiguationData":[OSD([sQuery(id+"F9.wireOp",EDGE,"E8.sketch_text.stroke-250")])],"isStart":false});
            var Q23;
            Q23=makeQuery(id+"F10.opExtrude","CAP_EDGE",EDGE,{"disambiguationData":[OSD([sQuery(id+"F9.wireOp",EDGE,"E8.sketch_text.stroke-249")])],"isStart":false});
            var Q24;
            Q24=makeQuery(id+"F10.opExtrude","CAP_EDGE",EDGE,{"disambiguationData":[OSD([sQuery(id+"F9.wireOp",EDGE,"E8.sketch_text.stroke-248")])],"isStart":false});
            var Q25;
            Q25=makeQuery(id+"F10.opExtrude","CAP_EDGE",EDGE,{"disambiguationData":[OSD([sQuery(id+"F9.wireOp",EDGE,"E8.sketch_text.stroke-247")])],"isStart":false});
            var Q26;
            Q26=makeQuery(id+"F10.opExtrude","CAP_EDGE",EDGE,{"disambiguationData":[OSD([sQuery(id+"F9.wireOp",EDGE,"E8.sketch_text.stroke-246")])],"isStart":false});
            fillet(context, id + "F12", {"entities" : qUnion([Q0, Q1, Q2, Q3, Q4, Q5, Q6, Q7, Q8, Q9, Q10, Q11, Q12, Q13, Q14, Q15, Q16, Q17, Q18, Q19, Q20, Q21, Q22, Q23, Q24, Q25, Q26]), "radius" : 0.25 * mm, "tangentPropagation" : true, "allowEdgeOverflow" : false});
        }
    });
